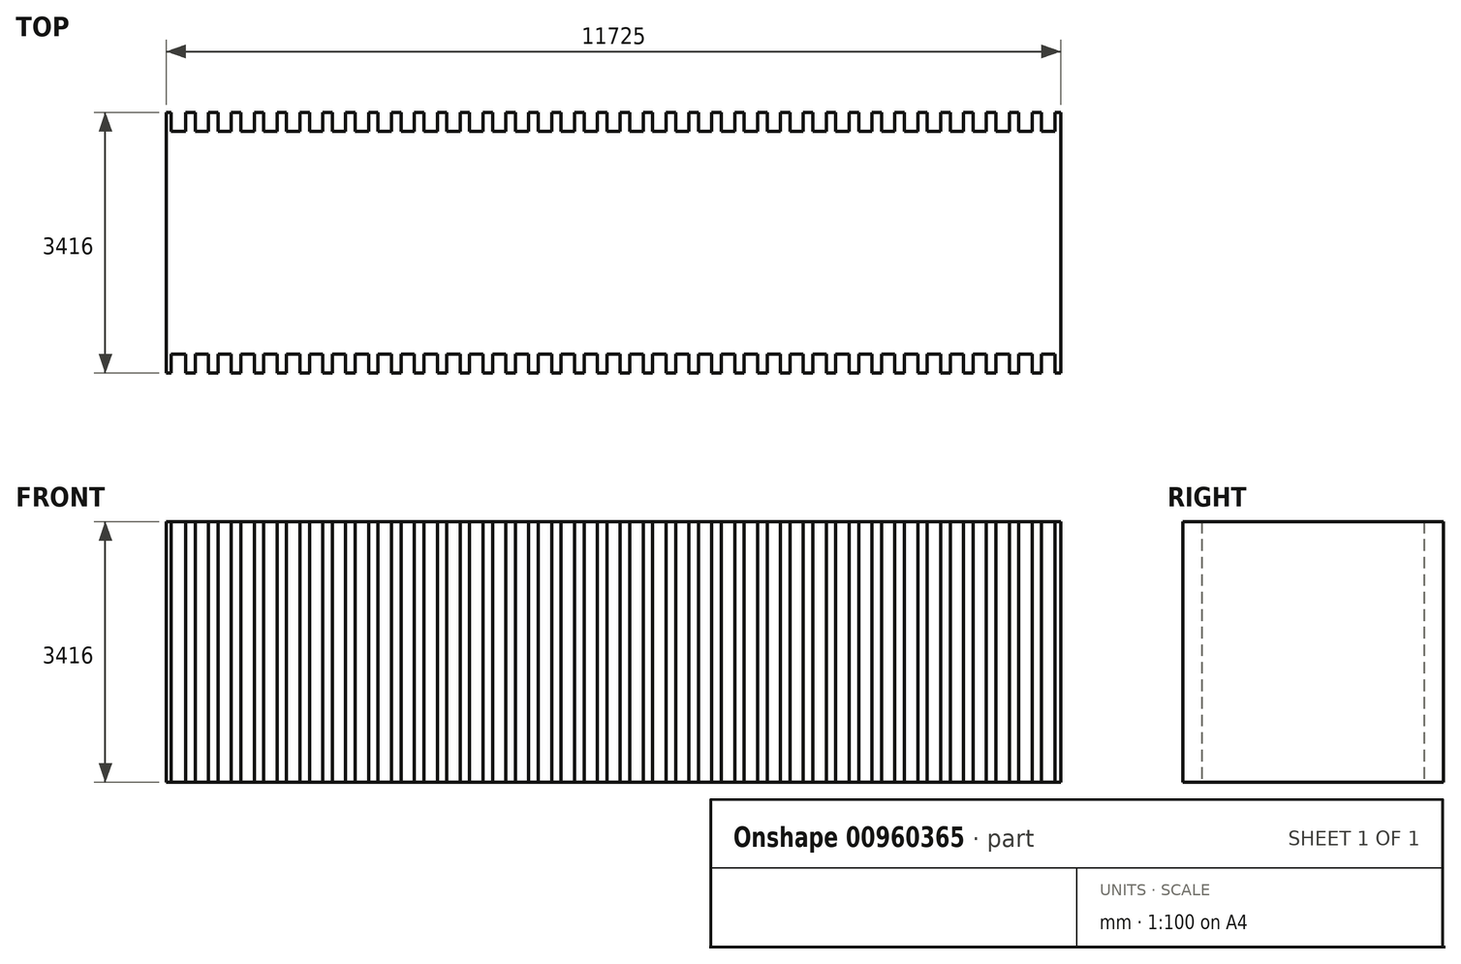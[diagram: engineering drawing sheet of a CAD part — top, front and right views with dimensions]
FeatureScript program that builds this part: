
annotation { "Feature Type Name" : "Feature", "Feature Type Description" : "" }
export const myFeature = defineFeature(function(context is Context, id is Id, definition is map)
    precondition{}
    {
        {
            var Q0;
            Q0=qCreatedBy(makeId("Top.planeOp"),FACE);
            var sketch = newSketch(context, id + "F0", { "sketchPlane" : qUnion([Q0])});
            skLineSegment(sketch, "E0.bottom", {"start": v(-25000, 7300) * mm, "end": v(25000, 7300) * mm});
            skLineSegment(sketch, "E0.top", {"start": v(-25000, -7300) * mm, "end": v(25000, -7300) * mm});
            skLineSegment(sketch, "E0.left", {"start": v(-25000, 7300) * mm, "end": v(-25000, -7300) * mm});
            skLineSegment(sketch, "E0.right", {"start": v(25000, 7300) * mm, "end": v(25000, -7300) * mm});
            skPoint(sketch, "E0.middle", {"position": v(0, 0) * mm});
            skSolve(sketch);
        }
        {
            var Q0;
            Q0=makeQuery(id+"F0.imprint","IMPRINT",FACE,{"disambiguationData":[TD([[makeQuery(id+"F0.imprint","IMPRINT",EDGE,{"derivedFrom":sQuery(id+"F0.wireOp",EDGE,"E0.bottom")}),-1.0]])]});
            var sketch = newSketch(context, id + "F1", { "sketchPlane" : qUnion([Q0])});
            skLineSegment(sketch, "E1", {"start": v(-20201.46, 5909) * mm, "end": v(-20138.96, 5909) * mm});
            skLineSegment(sketch, "E2", {"start": v(-20201.46, 5909) * mm, "end": v(-20201.46, 2493) * mm});
            skLineSegment(sketch, "E3", {"start": v(-20201.46, 2493) * mm, "end": v(-20138.96, 2493) * mm});
            skLineSegment(sketch, "E4", {"start": v(-8476.46, 2493) * mm, "end": v(-8476.46, 5909) * mm});
            skLineSegment(sketch, "E5.0", {"start": v(-20138.96, 5909) * mm, "end": v(-20138.96, 2493) * mm});
            skLineSegment(sketch, "E6.0", {"start": v(-19951.46, 5909) * mm, "end": v(-19951.46, 2493) * mm});
            skLineSegment(sketch, "E7.0", {"start": v(-19651.46, 5909) * mm, "end": v(-19651.46, 2493) * mm});
            skLineSegment(sketch, "E8.0", {"start": v(-19351.46, 5909) * mm, "end": v(-19351.46, 2493) * mm});
            skLineSegment(sketch, "E9.0", {"start": v(-19051.46, 5909) * mm, "end": v(-19051.46, 2493) * mm});
            skLineSegment(sketch, "E10.0", {"start": v(-18751.46, 5909) * mm, "end": v(-18751.46, 2493) * mm});
            skLineSegment(sketch, "E11.0", {"start": v(-18451.46, 5909) * mm, "end": v(-18451.46, 2493) * mm});
            skLineSegment(sketch, "E12.0", {"start": v(-18151.46, 5909) * mm, "end": v(-18151.46, 2493) * mm});
            skLineSegment(sketch, "E13.0", {"start": v(-17851.46, 5909) * mm, "end": v(-17851.46, 2493) * mm});
            skLineSegment(sketch, "E14.0", {"start": v(-17551.46, 5909) * mm, "end": v(-17551.46, 2493) * mm});
            skLineSegment(sketch, "E15.0", {"start": v(-17251.46, 5909) * mm, "end": v(-17251.46, 2493) * mm});
            skLineSegment(sketch, "E16.0", {"start": v(-16951.46, 5909) * mm, "end": v(-16951.46, 2493) * mm});
            skLineSegment(sketch, "E17.0", {"start": v(-16651.46, 5909) * mm, "end": v(-16651.46, 2493) * mm});
            skLineSegment(sketch, "E18.0", {"start": v(-16351.46, 5909) * mm, "end": v(-16351.46, 2493) * mm});
            skLineSegment(sketch, "E19.0", {"start": v(-16051.46, 5909) * mm, "end": v(-16051.46, 2493) * mm});
            skLineSegment(sketch, "E20.0", {"start": v(-15751.46, 5909) * mm, "end": v(-15751.46, 2493) * mm});
            skLineSegment(sketch, "E21.0", {"start": v(-25005, 7305) * mm, "end": v(-25005, -7305) * mm});
            skLineSegment(sketch, "E21.1", {"start": v(25005, 7305) * mm, "end": v(-25005, 7305) * mm});
            skLineSegment(sketch, "E21.2", {"start": v(25005, -7305) * mm, "end": v(25005, 7305) * mm});
            skLineSegment(sketch, "E21.3", {"start": v(-25005, -7305) * mm, "end": v(25005, -7305) * mm});
            skLineSegment(sketch, "E22.0", {"start": v(-15451.46, 5909) * mm, "end": v(-15451.46, 2493) * mm});
            skLineSegment(sketch, "E23.0", {"start": v(-15151.46, 5909) * mm, "end": v(-15151.46, 2493) * mm});
            skLineSegment(sketch, "E24.0", {"start": v(-14851.46, 5909) * mm, "end": v(-14851.46, 2493) * mm});
            skLineSegment(sketch, "E25.0", {"start": v(-14551.46, 5909) * mm, "end": v(-14551.46, 2493) * mm});
            skLineSegment(sketch, "E26.0", {"start": v(-14251.46, 5909) * mm, "end": v(-14251.46, 2493) * mm});
            skLineSegment(sketch, "E27.0", {"start": v(-13951.46, 5909) * mm, "end": v(-13951.46, 2493) * mm});
            skLineSegment(sketch, "E28.0", {"start": v(-13651.46, 5909) * mm, "end": v(-13651.46, 2493) * mm});
            skLineSegment(sketch, "E29.0", {"start": v(-13351.46, 5909) * mm, "end": v(-13351.46, 2493) * mm});
            skLineSegment(sketch, "E30.0", {"start": v(-13051.46, 5909) * mm, "end": v(-13051.46, 2493) * mm});
            skLineSegment(sketch, "E31.0", {"start": v(-12751.46, 5909) * mm, "end": v(-12751.46, 2493) * mm});
            skLineSegment(sketch, "E32.0", {"start": v(-12451.46, 5909) * mm, "end": v(-12451.46, 2493) * mm});
            skLineSegment(sketch, "E33.0", {"start": v(-12151.46, 5909) * mm, "end": v(-12151.46, 2493) * mm});
            skLineSegment(sketch, "E34.0", {"start": v(-11851.46, 5909) * mm, "end": v(-11851.46, 2493) * mm});
            skLineSegment(sketch, "E35.0", {"start": v(-11551.46, 5909) * mm, "end": v(-11551.46, 2493) * mm});
            skLineSegment(sketch, "E36.0", {"start": v(-11251.46, 5909) * mm, "end": v(-11251.46, 2493) * mm});
            skLineSegment(sketch, "E37.0", {"start": v(-10951.46, 5909) * mm, "end": v(-10951.46, 2493) * mm});
            skLineSegment(sketch, "E38.0", {"start": v(-10651.46, 5909) * mm, "end": v(-10651.46, 2493) * mm});
            skLineSegment(sketch, "E39.0", {"start": v(-10351.46, 5909) * mm, "end": v(-10351.46, 2493) * mm});
            skLineSegment(sketch, "E40.0", {"start": v(-10051.46, 5909) * mm, "end": v(-10051.46, 2493) * mm});
            skLineSegment(sketch, "E41.0", {"start": v(-9751.46, 5909) * mm, "end": v(-9751.46, 2493) * mm});
            skLineSegment(sketch, "E42.0", {"start": v(-9451.46, 5909) * mm, "end": v(-9451.46, 2493) * mm});
            skLineSegment(sketch, "E43.0", {"start": v(-9151.46, 5909) * mm, "end": v(-9151.46, 2493) * mm});
            skLineSegment(sketch, "E44.0", {"start": v(-8851.46, 5909) * mm, "end": v(-8851.46, 2493) * mm});
            skLineSegment(sketch, "E45.0", {"start": v(-8551.46, 5909) * mm, "end": v(-8551.46, 2493) * mm});
            skLineSegment(sketch, "E46.0", {"start": v(-19826.46, 5909) * mm, "end": v(-19826.46, 2493) * mm});
            skLineSegment(sketch, "E47.0", {"start": v(-19526.46, 5909) * mm, "end": v(-19526.46, 2493) * mm});
            skLineSegment(sketch, "E48.0", {"start": v(-19226.46, 5909) * mm, "end": v(-19226.46, 2493) * mm});
            skLineSegment(sketch, "E49.0", {"start": v(-18926.46, 5909) * mm, "end": v(-18926.46, 2493) * mm});
            skLineSegment(sketch, "E50.0", {"start": v(-18626.46, 5909) * mm, "end": v(-18626.46, 2493) * mm});
            skLineSegment(sketch, "E51.0", {"start": v(-18326.46, 5909) * mm, "end": v(-18326.46, 2493) * mm});
            skLineSegment(sketch, "E52.0", {"start": v(-18026.46, 5909) * mm, "end": v(-18026.46, 2493) * mm});
            skLineSegment(sketch, "E53.0", {"start": v(-17726.46, 5909) * mm, "end": v(-17726.46, 2493) * mm});
            skLineSegment(sketch, "E54.0", {"start": v(-17426.46, 5909) * mm, "end": v(-17426.46, 2493) * mm});
            skLineSegment(sketch, "E55.0", {"start": v(-17126.46, 5909) * mm, "end": v(-17126.46, 2493) * mm});
            skLineSegment(sketch, "E56.0", {"start": v(-16826.46, 5909) * mm, "end": v(-16826.46, 2493) * mm});
            skLineSegment(sketch, "E57.0", {"start": v(-16526.46, 5909) * mm, "end": v(-16526.46, 2493) * mm});
            skLineSegment(sketch, "E58.0", {"start": v(-16226.46, 5909) * mm, "end": v(-16226.46, 2493) * mm});
            skLineSegment(sketch, "E59.0", {"start": v(-15926.46, 5909) * mm, "end": v(-15926.46, 2493) * mm});
            skLineSegment(sketch, "E60.0", {"start": v(-15626.46, 5909) * mm, "end": v(-15626.46, 2493) * mm});
            skLineSegment(sketch, "E61.0", {"start": v(-15326.46, 5909) * mm, "end": v(-15326.46, 2493) * mm});
            skLineSegment(sketch, "E62.0", {"start": v(-15026.46, 5909) * mm, "end": v(-15026.46, 2493) * mm});
            skLineSegment(sketch, "E63.0", {"start": v(-14726.46, 5909) * mm, "end": v(-14726.46, 2493) * mm});
            skLineSegment(sketch, "E64.0", {"start": v(-14426.46, 5909) * mm, "end": v(-14426.46, 2493) * mm});
            skLineSegment(sketch, "E65.0", {"start": v(-14126.46, 5909) * mm, "end": v(-14126.46, 2493) * mm});
            skLineSegment(sketch, "E66.0", {"start": v(-13826.46, 5909) * mm, "end": v(-13826.46, 2493) * mm});
            skLineSegment(sketch, "E67.0", {"start": v(-13526.46, 5909) * mm, "end": v(-13526.46, 2493) * mm});
            skLineSegment(sketch, "E68.0", {"start": v(-13226.46, 5909) * mm, "end": v(-13226.46, 2493) * mm});
            skLineSegment(sketch, "E69.0", {"start": v(-12926.46, 5909) * mm, "end": v(-12926.46, 2493) * mm});
            skLineSegment(sketch, "E70.0", {"start": v(-12626.46, 5909) * mm, "end": v(-12626.46, 2493) * mm});
            skLineSegment(sketch, "E71.0", {"start": v(-12326.46, 5909) * mm, "end": v(-12326.46, 2493) * mm});
            skLineSegment(sketch, "E72.0", {"start": v(-12026.46, 5909) * mm, "end": v(-12026.46, 2493) * mm});
            skLineSegment(sketch, "E73.0", {"start": v(-11726.46, 5909) * mm, "end": v(-11726.46, 2493) * mm});
            skLineSegment(sketch, "E74.0", {"start": v(-11426.46, 5909) * mm, "end": v(-11426.46, 2493) * mm});
            skLineSegment(sketch, "E75.0", {"start": v(-11126.46, 5909) * mm, "end": v(-11126.46, 2493) * mm});
            skLineSegment(sketch, "E76.0", {"start": v(-10826.46, 5909) * mm, "end": v(-10826.46, 2493) * mm});
            skLineSegment(sketch, "E77.0", {"start": v(-10526.46, 5909) * mm, "end": v(-10526.46, 2493) * mm});
            skLineSegment(sketch, "E78.0", {"start": v(-10226.46, 5909) * mm, "end": v(-10226.46, 2493) * mm});
            skLineSegment(sketch, "E79.0", {"start": v(-9926.46, 5909) * mm, "end": v(-9926.46, 2493) * mm});
            skLineSegment(sketch, "E80.0", {"start": v(-9626.46, 5909) * mm, "end": v(-9626.46, 2493) * mm});
            skLineSegment(sketch, "E81.0", {"start": v(-9326.46, 5909) * mm, "end": v(-9326.46, 2493) * mm});
            skLineSegment(sketch, "E82.0", {"start": v(-9026.46, 5909) * mm, "end": v(-9026.46, 2493) * mm});
            skLineSegment(sketch, "E83.0", {"start": v(-8726.46, 5909) * mm, "end": v(-8726.46, 2493) * mm});
            skLineSegment(sketch, "E84", {"start": v(-20201.46, 5659) * mm, "end": v(-8476.46, 5659) * mm});
            skLineSegment(sketch, "E85", {"start": v(-20201.46, 2743) * mm, "end": v(-8476.46, 2743) * mm});
            skLineSegment(sketch, "E86.trimOffspring", {"start": v(-8551.46, 5909) * mm, "end": v(-8476.46, 5909) * mm});
            skLineSegment(sketch, "E87.trimOffspring", {"start": v(-8851.46, 5909) * mm, "end": v(-8726.46, 5909) * mm});
            skLineSegment(sketch, "E88.trimOffspring", {"start": v(-9151.46, 5909) * mm, "end": v(-9026.46, 5909) * mm});
            skLineSegment(sketch, "E89.trimOffspring", {"start": v(-9451.46, 5909) * mm, "end": v(-9326.46, 5909) * mm});
            skLineSegment(sketch, "E90.trimOffspring", {"start": v(-9751.46, 5909) * mm, "end": v(-9626.46, 5909) * mm});
            skLineSegment(sketch, "E91.trimOffspring", {"start": v(-10051.46, 5909) * mm, "end": v(-9926.46, 5909) * mm});
            skLineSegment(sketch, "E92.trimOffspring", {"start": v(-10351.46, 5909) * mm, "end": v(-10226.46, 5909) * mm});
            skLineSegment(sketch, "E93.trimOffspring", {"start": v(-10651.46, 5909) * mm, "end": v(-10526.46, 5909) * mm});
            skLineSegment(sketch, "E94.trimOffspring", {"start": v(-10951.46, 5909) * mm, "end": v(-10826.46, 5909) * mm});
            skLineSegment(sketch, "E95.trimOffspring", {"start": v(-11251.46, 5909) * mm, "end": v(-11126.46, 5909) * mm});
            skLineSegment(sketch, "E96.trimOffspring", {"start": v(-11551.46, 5909) * mm, "end": v(-11426.46, 5909) * mm});
            skLineSegment(sketch, "E97.trimOffspring", {"start": v(-11851.46, 5909) * mm, "end": v(-11726.46, 5909) * mm});
            skLineSegment(sketch, "E98.trimOffspring", {"start": v(-12151.46, 5909) * mm, "end": v(-12026.46, 5909) * mm});
            skLineSegment(sketch, "E99.trimOffspring", {"start": v(-12451.46, 5909) * mm, "end": v(-12326.46, 5909) * mm});
            skLineSegment(sketch, "E100.trimOffspring", {"start": v(-12751.46, 5909) * mm, "end": v(-12626.46, 5909) * mm});
            skLineSegment(sketch, "E101.trimOffspring", {"start": v(-13051.46, 5909) * mm, "end": v(-12926.46, 5909) * mm});
            skLineSegment(sketch, "E102.trimOffspring", {"start": v(-13351.46, 5909) * mm, "end": v(-13226.46, 5909) * mm});
            skLineSegment(sketch, "E103.trimOffspring", {"start": v(-13651.46, 5909) * mm, "end": v(-13526.46, 5909) * mm});
            skLineSegment(sketch, "E104.trimOffspring", {"start": v(-13951.46, 5909) * mm, "end": v(-13826.46, 5909) * mm});
            skLineSegment(sketch, "E105.trimOffspring", {"start": v(-14251.46, 5909) * mm, "end": v(-14126.46, 5909) * mm});
            skLineSegment(sketch, "E106.trimOffspring", {"start": v(-14551.46, 5909) * mm, "end": v(-14426.46, 5909) * mm});
            skLineSegment(sketch, "E107.trimOffspring", {"start": v(-14851.46, 5909) * mm, "end": v(-14726.46, 5909) * mm});
            skLineSegment(sketch, "E108.trimOffspring", {"start": v(-15151.46, 5909) * mm, "end": v(-15026.46, 5909) * mm});
            skLineSegment(sketch, "E109.trimOffspring", {"start": v(-15451.46, 5909) * mm, "end": v(-15326.46, 5909) * mm});
            skLineSegment(sketch, "E110.trimOffspring", {"start": v(-15751.46, 5909) * mm, "end": v(-15626.46, 5909) * mm});
            skLineSegment(sketch, "E111.trimOffspring", {"start": v(-16051.46, 5909) * mm, "end": v(-15926.46, 5909) * mm});
            skLineSegment(sketch, "E112.trimOffspring", {"start": v(-16351.46, 5909) * mm, "end": v(-16226.46, 5909) * mm});
            skLineSegment(sketch, "E113.trimOffspring", {"start": v(-16651.46, 5909) * mm, "end": v(-16526.46, 5909) * mm});
            skLineSegment(sketch, "E114.trimOffspring", {"start": v(-16951.46, 5909) * mm, "end": v(-16826.46, 5909) * mm});
            skLineSegment(sketch, "E115.trimOffspring", {"start": v(-17251.46, 5909) * mm, "end": v(-17126.46, 5909) * mm});
            skLineSegment(sketch, "E116.trimOffspring", {"start": v(-17551.46, 5909) * mm, "end": v(-17426.46, 5909) * mm});
            skLineSegment(sketch, "E117.trimOffspring", {"start": v(-17851.46, 5909) * mm, "end": v(-17726.46, 5909) * mm});
            skLineSegment(sketch, "E118.trimOffspring", {"start": v(-18151.46, 5909) * mm, "end": v(-18026.46, 5909) * mm});
            skLineSegment(sketch, "E119.trimOffspring", {"start": v(-18451.46, 5909) * mm, "end": v(-18326.46, 5909) * mm});
            skLineSegment(sketch, "E120.trimOffspring", {"start": v(-18751.46, 5909) * mm, "end": v(-18626.46, 5909) * mm});
            skLineSegment(sketch, "E121.trimOffspring", {"start": v(-19051.46, 5909) * mm, "end": v(-18926.46, 5909) * mm});
            skLineSegment(sketch, "E122.trimOffspring", {"start": v(-19351.46, 5909) * mm, "end": v(-19226.46, 5909) * mm});
            skLineSegment(sketch, "E123.trimOffspring", {"start": v(-19651.46, 5909) * mm, "end": v(-19526.46, 5909) * mm});
            skLineSegment(sketch, "E124.trimOffspring", {"start": v(-19951.46, 5909) * mm, "end": v(-19826.46, 5909) * mm});
            skLineSegment(sketch, "E125.trimOffspring", {"start": v(-19651.46, 2493) * mm, "end": v(-19526.46, 2493) * mm});
            skLineSegment(sketch, "E126.trimOffspring", {"start": v(-18751.46, 2493) * mm, "end": v(-18626.46, 2493) * mm});
            skLineSegment(sketch, "E127.trimOffspring", {"start": v(-17851.46, 2493) * mm, "end": v(-17726.46, 2493) * mm});
            skLineSegment(sketch, "E128.trimOffspring", {"start": v(-17251.46, 2493) * mm, "end": v(-17126.46, 2493) * mm});
            skLineSegment(sketch, "E129.trimOffspring", {"start": v(-16351.46, 2493) * mm, "end": v(-16226.46, 2493) * mm});
            skLineSegment(sketch, "E130.trimOffspring", {"start": v(-16951.46, 2493) * mm, "end": v(-16826.46, 2493) * mm});
            skLineSegment(sketch, "E131", {"start": v(-17551.46, 2493) * mm, "end": v(-17426.46, 2493) * mm});
            skLineSegment(sketch, "E132", {"start": v(-16651.46, 2493) * mm, "end": v(-16526.46, 2493) * mm});
            skLineSegment(sketch, "E133.trimOffspring", {"start": v(-15751.46, 2493) * mm, "end": v(-15626.46, 2493) * mm});
            skLineSegment(sketch, "E134.trimOffspring", {"start": v(-14551.46, 2493) * mm, "end": v(-14426.46, 2493) * mm});
            skLineSegment(sketch, "E135.trimOffspring", {"start": v(-15151.46, 2493) * mm, "end": v(-15026.46, 2493) * mm});
            skLineSegment(sketch, "E136.trimOffspring", {"start": v(-15451.46, 2493) * mm, "end": v(-15326.46, 2493) * mm});
            skLineSegment(sketch, "E137", {"start": v(-14851.46, 2493) * mm, "end": v(-14726.46, 2493) * mm});
            skLineSegment(sketch, "E138.trimOffspring", {"start": v(-13951.46, 2493) * mm, "end": v(-13826.46, 2493) * mm});
            skLineSegment(sketch, "E139.trimOffspring", {"start": v(-13351.46, 2493) * mm, "end": v(-13226.46, 2493) * mm});
            skLineSegment(sketch, "E140.trimOffspring", {"start": v(-13651.46, 2493) * mm, "end": v(-13526.46, 2493) * mm});
            skLineSegment(sketch, "E141", {"start": v(-14251.46, 2493) * mm, "end": v(-14126.46, 2493) * mm});
            skLineSegment(sketch, "E142.trimOffspring", {"start": v(-13051.46, 2493) * mm, "end": v(-12926.46, 2493) * mm});
            skLineSegment(sketch, "E143.trimOffspring", {"start": v(-12751.46, 2493) * mm, "end": v(-12626.46, 2493) * mm});
            skLineSegment(sketch, "E144.trimOffspring", {"start": v(-12151.46, 2493) * mm, "end": v(-12026.46, 2493) * mm});
            skLineSegment(sketch, "E145.trimOffspring", {"start": v(-11551.46, 2493) * mm, "end": v(-11426.46, 2493) * mm});
            skLineSegment(sketch, "E146.trimOffspring", {"start": v(-11851.46, 2493) * mm, "end": v(-11726.46, 2493) * mm});
            skLineSegment(sketch, "E147.trimOffspring", {"start": v(-11251.46, 2493) * mm, "end": v(-11126.46, 2493) * mm});
            skLineSegment(sketch, "E148.trimOffspring", {"start": v(-10951.46, 2493) * mm, "end": v(-10826.46, 2493) * mm});
            skLineSegment(sketch, "E149.trimOffspring", {"start": v(-10651.46, 2493) * mm, "end": v(-10526.46, 2493) * mm});
            skLineSegment(sketch, "E150.trimOffspring", {"start": v(-9751.46, 2493) * mm, "end": v(-9626.46, 2493) * mm});
            skLineSegment(sketch, "E151.trimOffspring", {"start": v(-8851.46, 2493) * mm, "end": v(-8726.46, 2493) * mm});
            skLineSegment(sketch, "E152", {"start": v(-10351.46, 2493) * mm, "end": v(-10226.46, 2493) * mm});
            skLineSegment(sketch, "E153", {"start": v(-10051.46, 2493) * mm, "end": v(-9926.46, 2493) * mm});
            skLineSegment(sketch, "E154", {"start": v(-9151.46, 2493) * mm, "end": v(-9026.46, 2493) * mm});
            skLineSegment(sketch, "E155.trimOffspring", {"start": v(-9451.46, 2493) * mm, "end": v(-9326.46, 2493) * mm});
            skLineSegment(sketch, "E156.trimOffspring", {"start": v(-8551.46, 2493) * mm, "end": v(-8476.46, 2493) * mm});
            skLineSegment(sketch, "E157.trimOffspring", {"start": v(-18451.46, 2493) * mm, "end": v(-18326.46, 2493) * mm});
            skLineSegment(sketch, "E158.trimOffspring", {"start": v(-19351.46, 2493) * mm, "end": v(-19226.46, 2493) * mm});
            skLineSegment(sketch, "E159", {"start": v(-19051.46, 2493) * mm, "end": v(-18926.46, 2493) * mm});
            skLineSegment(sketch, "E160", {"start": v(-18151.46, 2493) * mm, "end": v(-18026.46, 2493) * mm});
            skLineSegment(sketch, "E161", {"start": v(-16051.46, 2493) * mm, "end": v(-15926.46, 2493) * mm});
            skLineSegment(sketch, "E162", {"start": v(-19951.46, 2493) * mm, "end": v(-19826.46, 2493) * mm});
            skLineSegment(sketch, "E163", {"start": v(-12451.46, 2493) * mm, "end": v(-12326.46, 2493) * mm});
            skSolve(sketch);
        }
        {
            var Q0;
            {var subQ0=sQuery(id+"F1.wireOp",EDGE,"E88.trimOffspring");Q0=makeQuery(id+"F1.imprint","IMPRINT",FACE,{"disambiguationData":[TD([[makeQuery(id+"F1.imprint","IMPRINT",EDGE,{"derivedFrom":subQ0}),-1.0]])]});}
            var Q1;
            {var subQ0=sQuery(id+"F1.wireOp",EDGE,"E112.trimOffspring");Q1=makeQuery(id+"F1.imprint","IMPRINT",FACE,{"disambiguationData":[TD([[makeQuery(id+"F1.imprint","IMPRINT",EDGE,{"derivedFrom":subQ0}),-1.0]])]});}
            var Q2;
            {var subQ0=sQuery(id+"F1.wireOp",EDGE,"E84");var subQ1=sQuery(id+"F1.wireOp",EDGE,"E38.0");var subQ2=makeQuery(id+"F1.imprint","INTERSECT",VERTEX,{"derivedFrom":[subQ1,subQ0]});Q2=makeQuery(id+"F1.imprint","IMPRINT",FACE,{"disambiguationData":[TD([[makeQuery(id+"F1.imprint","IMPRINT",EDGE,{"disambiguationData":[TD([[subQ2,-1.0]])],"derivedFrom":subQ1}),1.0]])]});}
            var Q3;
            {var subQ0=sQuery(id+"F1.wireOp",EDGE,"E158.trimOffspring");Q3=makeQuery(id+"F1.imprint","IMPRINT",FACE,{"disambiguationData":[TD([[makeQuery(id+"F1.imprint","IMPRINT",EDGE,{"derivedFrom":subQ0}),1.0]])]});}
            var Q4;
            {var subQ0=sQuery(id+"F1.wireOp",EDGE,"E84");var subQ1=sQuery(id+"F1.wireOp",EDGE,"E18.0");var subQ2=makeQuery(id+"F1.imprint","INTERSECT",VERTEX,{"derivedFrom":[subQ1,subQ0]});Q4=makeQuery(id+"F1.imprint","IMPRINT",FACE,{"disambiguationData":[TD([[makeQuery(id+"F1.imprint","IMPRINT",EDGE,{"disambiguationData":[TD([[subQ2,-1.0]])],"derivedFrom":subQ1}),-1.0]])]});}
            var Q5;
            {var subQ0=sQuery(id+"F1.wireOp",EDGE,"E140.trimOffspring");Q5=makeQuery(id+"F1.imprint","IMPRINT",FACE,{"disambiguationData":[TD([[makeQuery(id+"F1.imprint","IMPRINT",EDGE,{"derivedFrom":subQ0}),1.0]])]});}
            var Q6;
            {var subQ0=sQuery(id+"F1.wireOp",EDGE,"E84");var subQ1=sQuery(id+"F1.wireOp",EDGE,"E35.0");var subQ2=makeQuery(id+"F1.imprint","INTERSECT",VERTEX,{"derivedFrom":[subQ1,subQ0]});Q6=makeQuery(id+"F1.imprint","IMPRINT",FACE,{"disambiguationData":[TD([[makeQuery(id+"F1.imprint","IMPRINT",EDGE,{"disambiguationData":[TD([[subQ2,-1.0]])],"derivedFrom":subQ1}),-1.0]])]});}
            var Q7;
            {var subQ0=sQuery(id+"F1.wireOp",EDGE,"E107.trimOffspring");Q7=makeQuery(id+"F1.imprint","IMPRINT",FACE,{"disambiguationData":[TD([[makeQuery(id+"F1.imprint","IMPRINT",EDGE,{"derivedFrom":subQ0}),-1.0]])]});}
            var Q8;
            {var subQ0=sQuery(id+"F1.wireOp",EDGE,"E129.trimOffspring");Q8=makeQuery(id+"F1.imprint","IMPRINT",FACE,{"disambiguationData":[TD([[makeQuery(id+"F1.imprint","IMPRINT",EDGE,{"derivedFrom":subQ0}),1.0]])]});}
            var Q9;
            {var subQ0=sQuery(id+"F1.wireOp",EDGE,"E120.trimOffspring");Q9=makeQuery(id+"F1.imprint","IMPRINT",FACE,{"disambiguationData":[TD([[makeQuery(id+"F1.imprint","IMPRINT",EDGE,{"derivedFrom":subQ0}),-1.0]])]});}
            var Q10;
            {var subQ0=sQuery(id+"F1.wireOp",EDGE,"E115.trimOffspring");Q10=makeQuery(id+"F1.imprint","IMPRINT",FACE,{"disambiguationData":[TD([[makeQuery(id+"F1.imprint","IMPRINT",EDGE,{"derivedFrom":subQ0}),-1.0]])]});}
            var Q11;
            {var subQ0=sQuery(id+"F1.wireOp",EDGE,"E138.trimOffspring");Q11=makeQuery(id+"F1.imprint","IMPRINT",FACE,{"disambiguationData":[TD([[makeQuery(id+"F1.imprint","IMPRINT",EDGE,{"derivedFrom":subQ0}),1.0]])]});}
            var Q12;
            {var subQ0=sQuery(id+"F1.wireOp",EDGE,"E84");var subQ1=sQuery(id+"F1.wireOp",EDGE,"E11.0");var subQ2=makeQuery(id+"F1.imprint","INTERSECT",VERTEX,{"derivedFrom":[subQ1,subQ0]});Q12=makeQuery(id+"F1.imprint","IMPRINT",FACE,{"disambiguationData":[TD([[makeQuery(id+"F1.imprint","IMPRINT",EDGE,{"disambiguationData":[TD([[subQ2,-1.0]])],"derivedFrom":subQ1}),1.0]])]});}
            var Q13;
            {var subQ0=sQuery(id+"F1.wireOp",EDGE,"E91.trimOffspring");Q13=makeQuery(id+"F1.imprint","IMPRINT",FACE,{"disambiguationData":[TD([[makeQuery(id+"F1.imprint","IMPRINT",EDGE,{"derivedFrom":subQ0}),-1.0]])]});}
            var Q14;
            {var subQ0=sQuery(id+"F1.wireOp",EDGE,"E84");var subQ1=sQuery(id+"F1.wireOp",EDGE,"E13.0");var subQ2=makeQuery(id+"F1.imprint","INTERSECT",VERTEX,{"derivedFrom":[subQ1,subQ0]});Q14=makeQuery(id+"F1.imprint","IMPRINT",FACE,{"disambiguationData":[TD([[makeQuery(id+"F1.imprint","IMPRINT",EDGE,{"disambiguationData":[TD([[subQ2,-1.0]])],"derivedFrom":subQ1}),-1.0]])]});}
            var Q15;
            {var subQ0=sQuery(id+"F1.wireOp",EDGE,"E84");var subQ1=sQuery(id+"F1.wireOp",EDGE,"E26.0");var subQ2=makeQuery(id+"F1.imprint","INTERSECT",VERTEX,{"derivedFrom":[subQ1,subQ0]});Q15=makeQuery(id+"F1.imprint","IMPRINT",FACE,{"disambiguationData":[TD([[makeQuery(id+"F1.imprint","IMPRINT",EDGE,{"disambiguationData":[TD([[subQ2,-1.0]])],"derivedFrom":subQ1}),-1.0]])]});}
            var Q16;
            {var subQ0=sQuery(id+"F1.wireOp",EDGE,"E121.trimOffspring");Q16=makeQuery(id+"F1.imprint","IMPRINT",FACE,{"disambiguationData":[TD([[makeQuery(id+"F1.imprint","IMPRINT",EDGE,{"derivedFrom":subQ0}),-1.0]])]});}
            var Q17;
            {var subQ0=sQuery(id+"F1.wireOp",EDGE,"E130.trimOffspring");Q17=makeQuery(id+"F1.imprint","IMPRINT",FACE,{"disambiguationData":[TD([[makeQuery(id+"F1.imprint","IMPRINT",EDGE,{"derivedFrom":subQ0}),1.0]])]});}
            var Q18;
            {var subQ0=sQuery(id+"F1.wireOp",EDGE,"E154");Q18=makeQuery(id+"F1.imprint","IMPRINT",FACE,{"disambiguationData":[TD([[makeQuery(id+"F1.imprint","IMPRINT",EDGE,{"derivedFrom":subQ0}),1.0]])]});}
            var Q19;
            {var subQ0=sQuery(id+"F1.wireOp",EDGE,"E151.trimOffspring");Q19=makeQuery(id+"F1.imprint","IMPRINT",FACE,{"disambiguationData":[TD([[makeQuery(id+"F1.imprint","IMPRINT",EDGE,{"derivedFrom":subQ0}),1.0]])]});}
            var Q20;
            {var subQ0=sQuery(id+"F1.wireOp",EDGE,"E84");var subQ1=sQuery(id+"F1.wireOp",EDGE,"E30.0");var subQ2=makeQuery(id+"F1.imprint","INTERSECT",VERTEX,{"derivedFrom":[subQ1,subQ0]});Q20=makeQuery(id+"F1.imprint","IMPRINT",FACE,{"disambiguationData":[TD([[makeQuery(id+"F1.imprint","IMPRINT",EDGE,{"disambiguationData":[TD([[subQ2,-1.0]])],"derivedFrom":subQ1}),-1.0]])]});}
            var Q21;
            {var subQ0=sQuery(id+"F1.wireOp",EDGE,"E84");var subQ1=sQuery(id+"F1.wireOp",EDGE,"E19.0");var subQ2=makeQuery(id+"F1.imprint","INTERSECT",VERTEX,{"derivedFrom":[subQ1,subQ0]});Q21=makeQuery(id+"F1.imprint","IMPRINT",FACE,{"disambiguationData":[TD([[makeQuery(id+"F1.imprint","IMPRINT",EDGE,{"disambiguationData":[TD([[subQ2,-1.0]])],"derivedFrom":subQ1}),1.0]])]});}
            var Q22;
            {var subQ0=sQuery(id+"F1.wireOp",EDGE,"E84");var subQ1=sQuery(id+"F1.wireOp",EDGE,"E14.0");var subQ2=makeQuery(id+"F1.imprint","INTERSECT",VERTEX,{"derivedFrom":[subQ1,subQ0]});Q22=makeQuery(id+"F1.imprint","IMPRINT",FACE,{"disambiguationData":[TD([[makeQuery(id+"F1.imprint","IMPRINT",EDGE,{"disambiguationData":[TD([[subQ2,-1.0]])],"derivedFrom":subQ1}),-1.0]])]});}
            var Q23;
            {var subQ0=sQuery(id+"F1.wireOp",EDGE,"E84");var subQ1=sQuery(id+"F1.wireOp",EDGE,"E12.0");var subQ2=makeQuery(id+"F1.imprint","INTERSECT",VERTEX,{"derivedFrom":[subQ1,subQ0]});Q23=makeQuery(id+"F1.imprint","IMPRINT",FACE,{"disambiguationData":[TD([[makeQuery(id+"F1.imprint","IMPRINT",EDGE,{"disambiguationData":[TD([[subQ2,-1.0]])],"derivedFrom":subQ1}),1.0]])]});}
            var Q24;
            {var subQ0=sQuery(id+"F1.wireOp",EDGE,"E143.trimOffspring");Q24=makeQuery(id+"F1.imprint","IMPRINT",FACE,{"disambiguationData":[TD([[makeQuery(id+"F1.imprint","IMPRINT",EDGE,{"derivedFrom":subQ0}),1.0]])]});}
            var Q25;
            {var subQ0=sQuery(id+"F1.wireOp",EDGE,"E161");Q25=makeQuery(id+"F1.imprint","IMPRINT",FACE,{"disambiguationData":[TD([[makeQuery(id+"F1.imprint","IMPRINT",EDGE,{"derivedFrom":subQ0}),1.0]])]});}
            var Q26;
            {var subQ0=sQuery(id+"F1.wireOp",EDGE,"E100.trimOffspring");Q26=makeQuery(id+"F1.imprint","IMPRINT",FACE,{"disambiguationData":[TD([[makeQuery(id+"F1.imprint","IMPRINT",EDGE,{"derivedFrom":subQ0}),-1.0]])]});}
            var Q27;
            {var subQ0=sQuery(id+"F1.wireOp",EDGE,"E84");var subQ1=sQuery(id+"F1.wireOp",EDGE,"E15.0");var subQ2=makeQuery(id+"F1.imprint","INTERSECT",VERTEX,{"derivedFrom":[subQ1,subQ0]});Q27=makeQuery(id+"F1.imprint","IMPRINT",FACE,{"disambiguationData":[TD([[makeQuery(id+"F1.imprint","IMPRINT",EDGE,{"disambiguationData":[TD([[subQ2,-1.0]])],"derivedFrom":subQ1}),-1.0]])]});}
            var Q28;
            {var subQ0=sQuery(id+"F1.wireOp",EDGE,"E84");var subQ1=sQuery(id+"F1.wireOp",EDGE,"E39.0");var subQ2=makeQuery(id+"F1.imprint","INTERSECT",VERTEX,{"derivedFrom":[subQ1,subQ0]});Q28=makeQuery(id+"F1.imprint","IMPRINT",FACE,{"disambiguationData":[TD([[makeQuery(id+"F1.imprint","IMPRINT",EDGE,{"disambiguationData":[TD([[subQ2,-1.0]])],"derivedFrom":subQ1}),1.0]])]});}
            var Q29;
            {var subQ0=sQuery(id+"F1.wireOp",EDGE,"E84");var subQ1=sQuery(id+"F1.wireOp",EDGE,"E36.0");var subQ2=makeQuery(id+"F1.imprint","INTERSECT",VERTEX,{"derivedFrom":[subQ1,subQ0]});Q29=makeQuery(id+"F1.imprint","IMPRINT",FACE,{"disambiguationData":[TD([[makeQuery(id+"F1.imprint","IMPRINT",EDGE,{"disambiguationData":[TD([[subQ2,-1.0]])],"derivedFrom":subQ1}),1.0]])]});}
            var Q30;
            {var subQ0=sQuery(id+"F1.wireOp",EDGE,"E84");var subQ1=sQuery(id+"F1.wireOp",EDGE,"E40.0");var subQ2=makeQuery(id+"F1.imprint","INTERSECT",VERTEX,{"derivedFrom":[subQ1,subQ0]});Q30=makeQuery(id+"F1.imprint","IMPRINT",FACE,{"disambiguationData":[TD([[makeQuery(id+"F1.imprint","IMPRINT",EDGE,{"disambiguationData":[TD([[subQ2,-1.0]])],"derivedFrom":subQ1}),1.0]])]});}
            var Q31;
            {var subQ0=sQuery(id+"F1.wireOp",EDGE,"E118.trimOffspring");Q31=makeQuery(id+"F1.imprint","IMPRINT",FACE,{"disambiguationData":[TD([[makeQuery(id+"F1.imprint","IMPRINT",EDGE,{"derivedFrom":subQ0}),-1.0]])]});}
            var Q32;
            {var subQ0=sQuery(id+"F1.wireOp",EDGE,"E84");var subQ1=sQuery(id+"F1.wireOp",EDGE,"E10.0");var subQ2=makeQuery(id+"F1.imprint","INTERSECT",VERTEX,{"derivedFrom":[subQ1,subQ0]});Q32=makeQuery(id+"F1.imprint","IMPRINT",FACE,{"disambiguationData":[TD([[makeQuery(id+"F1.imprint","IMPRINT",EDGE,{"disambiguationData":[TD([[subQ2,-1.0]])],"derivedFrom":subQ1}),-1.0]])]});}
            var Q33;
            {var subQ0=sQuery(id+"F1.wireOp",EDGE,"E84");var subQ1=sQuery(id+"F1.wireOp",EDGE,"E19.0");var subQ2=makeQuery(id+"F1.imprint","INTERSECT",VERTEX,{"derivedFrom":[subQ1,subQ0]});Q33=makeQuery(id+"F1.imprint","IMPRINT",FACE,{"disambiguationData":[TD([[makeQuery(id+"F1.imprint","IMPRINT",EDGE,{"disambiguationData":[TD([[subQ2,-1.0]])],"derivedFrom":subQ1}),-1.0]])]});}
            var Q34;
            {var subQ0=sQuery(id+"F1.wireOp",EDGE,"E84");var subQ1=sQuery(id+"F1.wireOp",EDGE,"E29.0");var subQ2=makeQuery(id+"F1.imprint","INTERSECT",VERTEX,{"derivedFrom":[subQ1,subQ0]});Q34=makeQuery(id+"F1.imprint","IMPRINT",FACE,{"disambiguationData":[TD([[makeQuery(id+"F1.imprint","IMPRINT",EDGE,{"disambiguationData":[TD([[subQ2,-1.0]])],"derivedFrom":subQ1}),-1.0]])]});}
            var Q35;
            {var subQ0=sQuery(id+"F1.wireOp",EDGE,"E84");var subQ1=sQuery(id+"F1.wireOp",EDGE,"E9.0");var subQ2=makeQuery(id+"F1.imprint","INTERSECT",VERTEX,{"derivedFrom":[subQ1,subQ0]});Q35=makeQuery(id+"F1.imprint","IMPRINT",FACE,{"disambiguationData":[TD([[makeQuery(id+"F1.imprint","IMPRINT",EDGE,{"disambiguationData":[TD([[subQ2,-1.0]])],"derivedFrom":subQ1}),-1.0]])]});}
            var Q36;
            {var subQ0=sQuery(id+"F1.wireOp",EDGE,"E102.trimOffspring");Q36=makeQuery(id+"F1.imprint","IMPRINT",FACE,{"disambiguationData":[TD([[makeQuery(id+"F1.imprint","IMPRINT",EDGE,{"derivedFrom":subQ0}),-1.0]])]});}
            var Q37;
            {var subQ0=sQuery(id+"F1.wireOp",EDGE,"E99.trimOffspring");Q37=makeQuery(id+"F1.imprint","IMPRINT",FACE,{"disambiguationData":[TD([[makeQuery(id+"F1.imprint","IMPRINT",EDGE,{"derivedFrom":subQ0}),-1.0]])]});}
            var Q38;
            {var subQ0=sQuery(id+"F1.wireOp",EDGE,"E117.trimOffspring");Q38=makeQuery(id+"F1.imprint","IMPRINT",FACE,{"disambiguationData":[TD([[makeQuery(id+"F1.imprint","IMPRINT",EDGE,{"derivedFrom":subQ0}),-1.0]])]});}
            var Q39;
            {var subQ0=sQuery(id+"F1.wireOp",EDGE,"E84");var subQ1=sQuery(id+"F1.wireOp",EDGE,"E17.0");var subQ2=makeQuery(id+"F1.imprint","INTERSECT",VERTEX,{"derivedFrom":[subQ1,subQ0]});Q39=makeQuery(id+"F1.imprint","IMPRINT",FACE,{"disambiguationData":[TD([[makeQuery(id+"F1.imprint","IMPRINT",EDGE,{"disambiguationData":[TD([[subQ2,-1.0]])],"derivedFrom":subQ1}),-1.0]])]});}
            var Q40;
            {var subQ0=sQuery(id+"F1.wireOp",EDGE,"E84");var subQ1=sQuery(id+"F1.wireOp",EDGE,"E33.0");var subQ2=makeQuery(id+"F1.imprint","INTERSECT",VERTEX,{"derivedFrom":[subQ1,subQ0]});Q40=makeQuery(id+"F1.imprint","IMPRINT",FACE,{"disambiguationData":[TD([[makeQuery(id+"F1.imprint","IMPRINT",EDGE,{"disambiguationData":[TD([[subQ2,-1.0]])],"derivedFrom":subQ1}),-1.0]])]});}
            var Q41;
            {var subQ0=sQuery(id+"F1.wireOp",EDGE,"E146.trimOffspring");Q41=makeQuery(id+"F1.imprint","IMPRINT",FACE,{"disambiguationData":[TD([[makeQuery(id+"F1.imprint","IMPRINT",EDGE,{"derivedFrom":subQ0}),1.0]])]});}
            var Q42;
            {var subQ0=sQuery(id+"F1.wireOp",EDGE,"E95.trimOffspring");Q42=makeQuery(id+"F1.imprint","IMPRINT",FACE,{"disambiguationData":[TD([[makeQuery(id+"F1.imprint","IMPRINT",EDGE,{"derivedFrom":subQ0}),-1.0]])]});}
            var Q43;
            {var subQ0=sQuery(id+"F1.wireOp",EDGE,"E134.trimOffspring");Q43=makeQuery(id+"F1.imprint","IMPRINT",FACE,{"disambiguationData":[TD([[makeQuery(id+"F1.imprint","IMPRINT",EDGE,{"derivedFrom":subQ0}),1.0]])]});}
            var Q44;
            {var subQ0=sQuery(id+"F1.wireOp",EDGE,"E122.trimOffspring");Q44=makeQuery(id+"F1.imprint","IMPRINT",FACE,{"disambiguationData":[TD([[makeQuery(id+"F1.imprint","IMPRINT",EDGE,{"derivedFrom":subQ0}),-1.0]])]});}
            var Q45;
            {var subQ0=sQuery(id+"F1.wireOp",EDGE,"E105.trimOffspring");Q45=makeQuery(id+"F1.imprint","IMPRINT",FACE,{"disambiguationData":[TD([[makeQuery(id+"F1.imprint","IMPRINT",EDGE,{"derivedFrom":subQ0}),-1.0]])]});}
            var Q46;
            {var subQ0=sQuery(id+"F1.wireOp",EDGE,"E84");var subQ1=sQuery(id+"F1.wireOp",EDGE,"E31.0");var subQ2=makeQuery(id+"F1.imprint","INTERSECT",VERTEX,{"derivedFrom":[subQ1,subQ0]});Q46=makeQuery(id+"F1.imprint","IMPRINT",FACE,{"disambiguationData":[TD([[makeQuery(id+"F1.imprint","IMPRINT",EDGE,{"disambiguationData":[TD([[subQ2,-1.0]])],"derivedFrom":subQ1}),-1.0]])]});}
            var Q47;
            {var subQ0=sQuery(id+"F1.wireOp",EDGE,"E84");var subQ1=sQuery(id+"F1.wireOp",EDGE,"E24.0");var subQ2=makeQuery(id+"F1.imprint","INTERSECT",VERTEX,{"derivedFrom":[subQ1,subQ0]});Q47=makeQuery(id+"F1.imprint","IMPRINT",FACE,{"disambiguationData":[TD([[makeQuery(id+"F1.imprint","IMPRINT",EDGE,{"disambiguationData":[TD([[subQ2,-1.0]])],"derivedFrom":subQ1}),1.0]])]});}
            var Q48;
            {var subQ0=sQuery(id+"F1.wireOp",EDGE,"E84");var subQ1=sQuery(id+"F1.wireOp",EDGE,"E43.0");var subQ2=makeQuery(id+"F1.imprint","INTERSECT",VERTEX,{"derivedFrom":[subQ1,subQ0]});Q48=makeQuery(id+"F1.imprint","IMPRINT",FACE,{"disambiguationData":[TD([[makeQuery(id+"F1.imprint","IMPRINT",EDGE,{"disambiguationData":[TD([[subQ2,-1.0]])],"derivedFrom":subQ1}),1.0]])]});}
            var Q49;
            {var subQ0=sQuery(id+"F1.wireOp",EDGE,"E123.trimOffspring");Q49=makeQuery(id+"F1.imprint","IMPRINT",FACE,{"disambiguationData":[TD([[makeQuery(id+"F1.imprint","IMPRINT",EDGE,{"derivedFrom":subQ0}),-1.0]])]});}
            var Q50;
            {var subQ0=sQuery(id+"F1.wireOp",EDGE,"E84");var subQ1=sQuery(id+"F1.wireOp",EDGE,"E43.0");var subQ2=makeQuery(id+"F1.imprint","INTERSECT",VERTEX,{"derivedFrom":[subQ1,subQ0]});Q50=makeQuery(id+"F1.imprint","IMPRINT",FACE,{"disambiguationData":[TD([[makeQuery(id+"F1.imprint","IMPRINT",EDGE,{"disambiguationData":[TD([[subQ2,-1.0]])],"derivedFrom":subQ1}),-1.0]])]});}
            var Q51;
            {var subQ0=sQuery(id+"F1.wireOp",EDGE,"E84");var subQ1=sQuery(id+"F1.wireOp",EDGE,"E32.0");var subQ2=makeQuery(id+"F1.imprint","INTERSECT",VERTEX,{"derivedFrom":[subQ1,subQ0]});Q51=makeQuery(id+"F1.imprint","IMPRINT",FACE,{"disambiguationData":[TD([[makeQuery(id+"F1.imprint","IMPRINT",EDGE,{"disambiguationData":[TD([[subQ2,-1.0]])],"derivedFrom":subQ1}),1.0]])]});}
            var Q52;
            {var subQ0=sQuery(id+"F1.wireOp",EDGE,"E133.trimOffspring");Q52=makeQuery(id+"F1.imprint","IMPRINT",FACE,{"disambiguationData":[TD([[makeQuery(id+"F1.imprint","IMPRINT",EDGE,{"derivedFrom":subQ0}),1.0]])]});}
            var Q53;
            {var subQ0=sQuery(id+"F1.wireOp",EDGE,"E84");var subQ1=sQuery(id+"F1.wireOp",EDGE,"E37.0");var subQ2=makeQuery(id+"F1.imprint","INTERSECT",VERTEX,{"derivedFrom":[subQ1,subQ0]});Q53=makeQuery(id+"F1.imprint","IMPRINT",FACE,{"disambiguationData":[TD([[makeQuery(id+"F1.imprint","IMPRINT",EDGE,{"disambiguationData":[TD([[subQ2,-1.0]])],"derivedFrom":subQ1}),1.0]])]});}
            var Q54;
            {var subQ0=sQuery(id+"F1.wireOp",EDGE,"E141");Q54=makeQuery(id+"F1.imprint","IMPRINT",FACE,{"disambiguationData":[TD([[makeQuery(id+"F1.imprint","IMPRINT",EDGE,{"derivedFrom":subQ0}),1.0]])]});}
            var Q55;
            {var subQ0=sQuery(id+"F1.wireOp",EDGE,"E84");var subQ1=sQuery(id+"F1.wireOp",EDGE,"E17.0");var subQ2=makeQuery(id+"F1.imprint","INTERSECT",VERTEX,{"derivedFrom":[subQ1,subQ0]});Q55=makeQuery(id+"F1.imprint","IMPRINT",FACE,{"disambiguationData":[TD([[makeQuery(id+"F1.imprint","IMPRINT",EDGE,{"disambiguationData":[TD([[subQ2,-1.0]])],"derivedFrom":subQ1}),1.0]])]});}
            var Q56;
            {var subQ0=sQuery(id+"F1.wireOp",EDGE,"E127.trimOffspring");Q56=makeQuery(id+"F1.imprint","IMPRINT",FACE,{"disambiguationData":[TD([[makeQuery(id+"F1.imprint","IMPRINT",EDGE,{"derivedFrom":subQ0}),1.0]])]});}
            var Q57;
            {var subQ0=sQuery(id+"F1.wireOp",EDGE,"E84");var subQ1=sQuery(id+"F1.wireOp",EDGE,"E8.0");var subQ2=makeQuery(id+"F1.imprint","INTERSECT",VERTEX,{"derivedFrom":[subQ1,subQ0]});Q57=makeQuery(id+"F1.imprint","IMPRINT",FACE,{"disambiguationData":[TD([[makeQuery(id+"F1.imprint","IMPRINT",EDGE,{"disambiguationData":[TD([[subQ2,-1.0]])],"derivedFrom":subQ1}),-1.0]])]});}
            var Q58;
            {var subQ0=sQuery(id+"F1.wireOp",EDGE,"E84");var subQ1=sQuery(id+"F1.wireOp",EDGE,"E35.0");var subQ2=makeQuery(id+"F1.imprint","INTERSECT",VERTEX,{"derivedFrom":[subQ1,subQ0]});Q58=makeQuery(id+"F1.imprint","IMPRINT",FACE,{"disambiguationData":[TD([[makeQuery(id+"F1.imprint","IMPRINT",EDGE,{"disambiguationData":[TD([[subQ2,-1.0]])],"derivedFrom":subQ1}),1.0]])]});}
            var Q59;
            {var subQ0=sQuery(id+"F1.wireOp",EDGE,"E84");var subQ1=sQuery(id+"F1.wireOp",EDGE,"E27.0");var subQ2=makeQuery(id+"F1.imprint","INTERSECT",VERTEX,{"derivedFrom":[subQ1,subQ0]});Q59=makeQuery(id+"F1.imprint","IMPRINT",FACE,{"disambiguationData":[TD([[makeQuery(id+"F1.imprint","IMPRINT",EDGE,{"disambiguationData":[TD([[subQ2,-1.0]])],"derivedFrom":subQ1}),1.0]])]});}
            var Q60;
            {var subQ0=sQuery(id+"F1.wireOp",EDGE,"E84");var subQ1=sQuery(id+"F1.wireOp",EDGE,"E42.0");var subQ2=makeQuery(id+"F1.imprint","INTERSECT",VERTEX,{"derivedFrom":[subQ1,subQ0]});Q60=makeQuery(id+"F1.imprint","IMPRINT",FACE,{"disambiguationData":[TD([[makeQuery(id+"F1.imprint","IMPRINT",EDGE,{"disambiguationData":[TD([[subQ2,-1.0]])],"derivedFrom":subQ1}),-1.0]])]});}
            var Q61;
            {var subQ0=sQuery(id+"F1.wireOp",EDGE,"E93.trimOffspring");Q61=makeQuery(id+"F1.imprint","IMPRINT",FACE,{"disambiguationData":[TD([[makeQuery(id+"F1.imprint","IMPRINT",EDGE,{"derivedFrom":subQ0}),-1.0]])]});}
            var Q62;
            {var subQ0=sQuery(id+"F1.wireOp",EDGE,"E84");var subQ1=sQuery(id+"F1.wireOp",EDGE,"E28.0");var subQ2=makeQuery(id+"F1.imprint","INTERSECT",VERTEX,{"derivedFrom":[subQ1,subQ0]});Q62=makeQuery(id+"F1.imprint","IMPRINT",FACE,{"disambiguationData":[TD([[makeQuery(id+"F1.imprint","IMPRINT",EDGE,{"disambiguationData":[TD([[subQ2,-1.0]])],"derivedFrom":subQ1}),-1.0]])]});}
            var Q63;
            {var subQ0=sQuery(id+"F1.wireOp",EDGE,"E84");var subQ1=sQuery(id+"F1.wireOp",EDGE,"E12.0");var subQ2=makeQuery(id+"F1.imprint","INTERSECT",VERTEX,{"derivedFrom":[subQ1,subQ0]});Q63=makeQuery(id+"F1.imprint","IMPRINT",FACE,{"disambiguationData":[TD([[makeQuery(id+"F1.imprint","IMPRINT",EDGE,{"disambiguationData":[TD([[subQ2,-1.0]])],"derivedFrom":subQ1}),-1.0]])]});}
            var Q64;
            {var subQ0=sQuery(id+"F1.wireOp",EDGE,"E84");var subQ1=sQuery(id+"F1.wireOp",EDGE,"E26.0");var subQ2=makeQuery(id+"F1.imprint","INTERSECT",VERTEX,{"derivedFrom":[subQ1,subQ0]});Q64=makeQuery(id+"F1.imprint","IMPRINT",FACE,{"disambiguationData":[TD([[makeQuery(id+"F1.imprint","IMPRINT",EDGE,{"disambiguationData":[TD([[subQ2,-1.0]])],"derivedFrom":subQ1}),1.0]])]});}
            var Q65;
            {var subQ0=sQuery(id+"F1.wireOp",EDGE,"E148.trimOffspring");Q65=makeQuery(id+"F1.imprint","IMPRINT",FACE,{"disambiguationData":[TD([[makeQuery(id+"F1.imprint","IMPRINT",EDGE,{"derivedFrom":subQ0}),1.0]])]});}
            var Q66;
            {var subQ0=sQuery(id+"F1.wireOp",EDGE,"E142.trimOffspring");Q66=makeQuery(id+"F1.imprint","IMPRINT",FACE,{"disambiguationData":[TD([[makeQuery(id+"F1.imprint","IMPRINT",EDGE,{"derivedFrom":subQ0}),1.0]])]});}
            var Q67;
            {var subQ0=sQuery(id+"F1.wireOp",EDGE,"E106.trimOffspring");Q67=makeQuery(id+"F1.imprint","IMPRINT",FACE,{"disambiguationData":[TD([[makeQuery(id+"F1.imprint","IMPRINT",EDGE,{"derivedFrom":subQ0}),-1.0]])]});}
            var Q68;
            {var subQ0=sQuery(id+"F1.wireOp",EDGE,"E84");var subQ1=sQuery(id+"F1.wireOp",EDGE,"E28.0");var subQ2=makeQuery(id+"F1.imprint","INTERSECT",VERTEX,{"derivedFrom":[subQ1,subQ0]});Q68=makeQuery(id+"F1.imprint","IMPRINT",FACE,{"disambiguationData":[TD([[makeQuery(id+"F1.imprint","IMPRINT",EDGE,{"disambiguationData":[TD([[subQ2,-1.0]])],"derivedFrom":subQ1}),1.0]])]});}
            var Q69;
            {var subQ0=sQuery(id+"F1.wireOp",EDGE,"E92.trimOffspring");Q69=makeQuery(id+"F1.imprint","IMPRINT",FACE,{"disambiguationData":[TD([[makeQuery(id+"F1.imprint","IMPRINT",EDGE,{"derivedFrom":subQ0}),-1.0]])]});}
            var Q70;
            {var subQ0=sQuery(id+"F1.wireOp",EDGE,"E84");var subQ1=sQuery(id+"F1.wireOp",EDGE,"E7.0");var subQ2=makeQuery(id+"F1.imprint","INTERSECT",VERTEX,{"derivedFrom":[subQ1,subQ0]});Q70=makeQuery(id+"F1.imprint","IMPRINT",FACE,{"disambiguationData":[TD([[makeQuery(id+"F1.imprint","IMPRINT",EDGE,{"disambiguationData":[TD([[subQ2,-1.0]])],"derivedFrom":subQ1}),-1.0]])]});}
            var Q71;
            {var subQ0=sQuery(id+"F1.wireOp",EDGE,"E84");var subQ1=sQuery(id+"F1.wireOp",EDGE,"E31.0");var subQ2=makeQuery(id+"F1.imprint","INTERSECT",VERTEX,{"derivedFrom":[subQ1,subQ0]});Q71=makeQuery(id+"F1.imprint","IMPRINT",FACE,{"disambiguationData":[TD([[makeQuery(id+"F1.imprint","IMPRINT",EDGE,{"disambiguationData":[TD([[subQ2,-1.0]])],"derivedFrom":subQ1}),1.0]])]});}
            var Q72;
            {var subQ0=sQuery(id+"F1.wireOp",EDGE,"E152");Q72=makeQuery(id+"F1.imprint","IMPRINT",FACE,{"disambiguationData":[TD([[makeQuery(id+"F1.imprint","IMPRINT",EDGE,{"derivedFrom":subQ0}),1.0]])]});}
            var Q73;
            {var subQ0=sQuery(id+"F1.wireOp",EDGE,"E87.trimOffspring");Q73=makeQuery(id+"F1.imprint","IMPRINT",FACE,{"disambiguationData":[TD([[makeQuery(id+"F1.imprint","IMPRINT",EDGE,{"derivedFrom":subQ0}),-1.0]])]});}
            var Q74;
            {var subQ0=sQuery(id+"F1.wireOp",EDGE,"E84");var subQ1=sQuery(id+"F1.wireOp",EDGE,"E22.0");var subQ2=makeQuery(id+"F1.imprint","INTERSECT",VERTEX,{"derivedFrom":[subQ1,subQ0]});Q74=makeQuery(id+"F1.imprint","IMPRINT",FACE,{"disambiguationData":[TD([[makeQuery(id+"F1.imprint","IMPRINT",EDGE,{"disambiguationData":[TD([[subQ2,-1.0]])],"derivedFrom":subQ1}),-1.0]])]});}
            var Q75;
            {var subQ0=sQuery(id+"F1.wireOp",EDGE,"E84");var subQ1=sQuery(id+"F1.wireOp",EDGE,"E44.0");var subQ2=makeQuery(id+"F1.imprint","INTERSECT",VERTEX,{"derivedFrom":[subQ1,subQ0]});Q75=makeQuery(id+"F1.imprint","IMPRINT",FACE,{"disambiguationData":[TD([[makeQuery(id+"F1.imprint","IMPRINT",EDGE,{"disambiguationData":[TD([[subQ2,-1.0]])],"derivedFrom":subQ1}),1.0]])]});}
            var Q76;
            {var subQ0=sQuery(id+"F1.wireOp",EDGE,"E84");var subQ1=sQuery(id+"F1.wireOp",EDGE,"E18.0");var subQ2=makeQuery(id+"F1.imprint","INTERSECT",VERTEX,{"derivedFrom":[subQ1,subQ0]});Q76=makeQuery(id+"F1.imprint","IMPRINT",FACE,{"disambiguationData":[TD([[makeQuery(id+"F1.imprint","IMPRINT",EDGE,{"disambiguationData":[TD([[subQ2,-1.0]])],"derivedFrom":subQ1}),1.0]])]});}
            var Q77;
            {var subQ0=sQuery(id+"F1.wireOp",EDGE,"E96.trimOffspring");Q77=makeQuery(id+"F1.imprint","IMPRINT",FACE,{"disambiguationData":[TD([[makeQuery(id+"F1.imprint","IMPRINT",EDGE,{"derivedFrom":subQ0}),-1.0]])]});}
            var Q78;
            {var subQ0=sQuery(id+"F1.wireOp",EDGE,"E139.trimOffspring");Q78=makeQuery(id+"F1.imprint","IMPRINT",FACE,{"disambiguationData":[TD([[makeQuery(id+"F1.imprint","IMPRINT",EDGE,{"derivedFrom":subQ0}),1.0]])]});}
            var Q79;
            {var subQ0=sQuery(id+"F1.wireOp",EDGE,"E84");var subQ1=sQuery(id+"F1.wireOp",EDGE,"E7.0");var subQ2=makeQuery(id+"F1.imprint","INTERSECT",VERTEX,{"derivedFrom":[subQ1,subQ0]});Q79=makeQuery(id+"F1.imprint","IMPRINT",FACE,{"disambiguationData":[TD([[makeQuery(id+"F1.imprint","IMPRINT",EDGE,{"disambiguationData":[TD([[subQ2,-1.0]])],"derivedFrom":subQ1}),1.0]])]});}
            var Q80;
            {var subQ0=sQuery(id+"F1.wireOp",EDGE,"E84");var subQ1=sQuery(id+"F1.wireOp",EDGE,"E30.0");var subQ2=makeQuery(id+"F1.imprint","INTERSECT",VERTEX,{"derivedFrom":[subQ1,subQ0]});Q80=makeQuery(id+"F1.imprint","IMPRINT",FACE,{"disambiguationData":[TD([[makeQuery(id+"F1.imprint","IMPRINT",EDGE,{"disambiguationData":[TD([[subQ2,-1.0]])],"derivedFrom":subQ1}),1.0]])]});}
            var Q81;
            {var subQ0=sQuery(id+"F1.wireOp",EDGE,"E125.trimOffspring");Q81=makeQuery(id+"F1.imprint","IMPRINT",FACE,{"disambiguationData":[TD([[makeQuery(id+"F1.imprint","IMPRINT",EDGE,{"derivedFrom":subQ0}),1.0]])]});}
            var Q82;
            {var subQ0=sQuery(id+"F1.wireOp",EDGE,"E124.trimOffspring");Q82=makeQuery(id+"F1.imprint","IMPRINT",FACE,{"disambiguationData":[TD([[makeQuery(id+"F1.imprint","IMPRINT",EDGE,{"derivedFrom":subQ0}),-1.0]])]});}
            var Q83;
            {var subQ0=sQuery(id+"F1.wireOp",EDGE,"E84");var subQ1=sQuery(id+"F1.wireOp",EDGE,"E27.0");var subQ2=makeQuery(id+"F1.imprint","INTERSECT",VERTEX,{"derivedFrom":[subQ1,subQ0]});Q83=makeQuery(id+"F1.imprint","IMPRINT",FACE,{"disambiguationData":[TD([[makeQuery(id+"F1.imprint","IMPRINT",EDGE,{"disambiguationData":[TD([[subQ2,-1.0]])],"derivedFrom":subQ1}),-1.0]])]});}
            var Q84;
            {var subQ0=sQuery(id+"F1.wireOp",EDGE,"E147.trimOffspring");Q84=makeQuery(id+"F1.imprint","IMPRINT",FACE,{"disambiguationData":[TD([[makeQuery(id+"F1.imprint","IMPRINT",EDGE,{"derivedFrom":subQ0}),1.0]])]});}
            var Q85;
            {var subQ0=sQuery(id+"F1.wireOp",EDGE,"E84");var subQ1=sQuery(id+"F1.wireOp",EDGE,"E37.0");var subQ2=makeQuery(id+"F1.imprint","INTERSECT",VERTEX,{"derivedFrom":[subQ1,subQ0]});Q85=makeQuery(id+"F1.imprint","IMPRINT",FACE,{"disambiguationData":[TD([[makeQuery(id+"F1.imprint","IMPRINT",EDGE,{"disambiguationData":[TD([[subQ2,-1.0]])],"derivedFrom":subQ1}),-1.0]])]});}
            var Q86;
            {var subQ0=sQuery(id+"F1.wireOp",EDGE,"E84");var subQ1=sQuery(id+"F1.wireOp",EDGE,"E32.0");var subQ2=makeQuery(id+"F1.imprint","INTERSECT",VERTEX,{"derivedFrom":[subQ1,subQ0]});Q86=makeQuery(id+"F1.imprint","IMPRINT",FACE,{"disambiguationData":[TD([[makeQuery(id+"F1.imprint","IMPRINT",EDGE,{"disambiguationData":[TD([[subQ2,-1.0]])],"derivedFrom":subQ1}),-1.0]])]});}
            var Q87;
            {var subQ0=sQuery(id+"F1.wireOp",EDGE,"E131");Q87=makeQuery(id+"F1.imprint","IMPRINT",FACE,{"disambiguationData":[TD([[makeQuery(id+"F1.imprint","IMPRINT",EDGE,{"derivedFrom":subQ0}),1.0]])]});}
            var Q88;
            {var subQ0=sQuery(id+"F1.wireOp",EDGE,"E84");var subQ1=sQuery(id+"F1.wireOp",EDGE,"E34.0");var subQ2=makeQuery(id+"F1.imprint","INTERSECT",VERTEX,{"derivedFrom":[subQ1,subQ0]});Q88=makeQuery(id+"F1.imprint","IMPRINT",FACE,{"disambiguationData":[TD([[makeQuery(id+"F1.imprint","IMPRINT",EDGE,{"disambiguationData":[TD([[subQ2,-1.0]])],"derivedFrom":subQ1}),-1.0]])]});}
            var Q89;
            {var subQ0=sQuery(id+"F1.wireOp",EDGE,"E84");var subQ1=sQuery(id+"F1.wireOp",EDGE,"E14.0");var subQ2=makeQuery(id+"F1.imprint","INTERSECT",VERTEX,{"derivedFrom":[subQ1,subQ0]});Q89=makeQuery(id+"F1.imprint","IMPRINT",FACE,{"disambiguationData":[TD([[makeQuery(id+"F1.imprint","IMPRINT",EDGE,{"disambiguationData":[TD([[subQ2,-1.0]])],"derivedFrom":subQ1}),1.0]])]});}
            var Q90;
            {var subQ0=sQuery(id+"F1.wireOp",EDGE,"E145.trimOffspring");Q90=makeQuery(id+"F1.imprint","IMPRINT",FACE,{"disambiguationData":[TD([[makeQuery(id+"F1.imprint","IMPRINT",EDGE,{"derivedFrom":subQ0}),1.0]])]});}
            var Q91;
            {var subQ0=sQuery(id+"F1.wireOp",EDGE,"E84");var subQ1=sQuery(id+"F1.wireOp",EDGE,"E44.0");var subQ2=makeQuery(id+"F1.imprint","INTERSECT",VERTEX,{"derivedFrom":[subQ1,subQ0]});Q91=makeQuery(id+"F1.imprint","IMPRINT",FACE,{"disambiguationData":[TD([[makeQuery(id+"F1.imprint","IMPRINT",EDGE,{"disambiguationData":[TD([[subQ2,-1.0]])],"derivedFrom":subQ1}),-1.0]])]});}
            var Q92;
            {var subQ0=sQuery(id+"F1.wireOp",EDGE,"E101.trimOffspring");Q92=makeQuery(id+"F1.imprint","IMPRINT",FACE,{"disambiguationData":[TD([[makeQuery(id+"F1.imprint","IMPRINT",EDGE,{"derivedFrom":subQ0}),-1.0]])]});}
            var Q93;
            {var subQ0=sQuery(id+"F1.wireOp",EDGE,"E84");var subQ1=sQuery(id+"F1.wireOp",EDGE,"E20.0");var subQ2=makeQuery(id+"F1.imprint","INTERSECT",VERTEX,{"derivedFrom":[subQ1,subQ0]});Q93=makeQuery(id+"F1.imprint","IMPRINT",FACE,{"disambiguationData":[TD([[makeQuery(id+"F1.imprint","IMPRINT",EDGE,{"disambiguationData":[TD([[subQ2,-1.0]])],"derivedFrom":subQ1}),-1.0]])]});}
            var Q94;
            {var subQ0=sQuery(id+"F1.wireOp",EDGE,"E89.trimOffspring");Q94=makeQuery(id+"F1.imprint","IMPRINT",FACE,{"disambiguationData":[TD([[makeQuery(id+"F1.imprint","IMPRINT",EDGE,{"derivedFrom":subQ0}),-1.0]])]});}
            var Q95;
            {var subQ0=sQuery(id+"F1.wireOp",EDGE,"E84");var subQ1=sQuery(id+"F1.wireOp",EDGE,"E36.0");var subQ2=makeQuery(id+"F1.imprint","INTERSECT",VERTEX,{"derivedFrom":[subQ1,subQ0]});Q95=makeQuery(id+"F1.imprint","IMPRINT",FACE,{"disambiguationData":[TD([[makeQuery(id+"F1.imprint","IMPRINT",EDGE,{"disambiguationData":[TD([[subQ2,-1.0]])],"derivedFrom":subQ1}),-1.0]])]});}
            var Q96;
            {var subQ0=sQuery(id+"F1.wireOp",EDGE,"E150.trimOffspring");Q96=makeQuery(id+"F1.imprint","IMPRINT",FACE,{"disambiguationData":[TD([[makeQuery(id+"F1.imprint","IMPRINT",EDGE,{"derivedFrom":subQ0}),1.0]])]});}
            var Q97;
            {var subQ0=sQuery(id+"F1.wireOp",EDGE,"E84");var subQ1=sQuery(id+"F1.wireOp",EDGE,"E34.0");var subQ2=makeQuery(id+"F1.imprint","INTERSECT",VERTEX,{"derivedFrom":[subQ1,subQ0]});Q97=makeQuery(id+"F1.imprint","IMPRINT",FACE,{"disambiguationData":[TD([[makeQuery(id+"F1.imprint","IMPRINT",EDGE,{"disambiguationData":[TD([[subQ2,-1.0]])],"derivedFrom":subQ1}),1.0]])]});}
            var Q98;
            {var subQ0=sQuery(id+"F1.wireOp",EDGE,"E103.trimOffspring");Q98=makeQuery(id+"F1.imprint","IMPRINT",FACE,{"disambiguationData":[TD([[makeQuery(id+"F1.imprint","IMPRINT",EDGE,{"derivedFrom":subQ0}),-1.0]])]});}
            var Q99;
            {var subQ0=sQuery(id+"F1.wireOp",EDGE,"E84");var subQ1=sQuery(id+"F1.wireOp",EDGE,"E16.0");var subQ2=makeQuery(id+"F1.imprint","INTERSECT",VERTEX,{"derivedFrom":[subQ1,subQ0]});Q99=makeQuery(id+"F1.imprint","IMPRINT",FACE,{"disambiguationData":[TD([[makeQuery(id+"F1.imprint","IMPRINT",EDGE,{"disambiguationData":[TD([[subQ2,-1.0]])],"derivedFrom":subQ1}),-1.0]])]});}
            var Q100;
            {var subQ0=sQuery(id+"F1.wireOp",EDGE,"E109.trimOffspring");Q100=makeQuery(id+"F1.imprint","IMPRINT",FACE,{"disambiguationData":[TD([[makeQuery(id+"F1.imprint","IMPRINT",EDGE,{"derivedFrom":subQ0}),-1.0]])]});}
            var Q101;
            {var subQ0=sQuery(id+"F1.wireOp",EDGE,"E155.trimOffspring");Q101=makeQuery(id+"F1.imprint","IMPRINT",FACE,{"disambiguationData":[TD([[makeQuery(id+"F1.imprint","IMPRINT",EDGE,{"derivedFrom":subQ0}),1.0]])]});}
            var Q102;
            {var subQ0=sQuery(id+"F1.wireOp",EDGE,"E90.trimOffspring");Q102=makeQuery(id+"F1.imprint","IMPRINT",FACE,{"disambiguationData":[TD([[makeQuery(id+"F1.imprint","IMPRINT",EDGE,{"derivedFrom":subQ0}),-1.0]])]});}
            var Q103;
            {var subQ0=sQuery(id+"F1.wireOp",EDGE,"E128.trimOffspring");Q103=makeQuery(id+"F1.imprint","IMPRINT",FACE,{"disambiguationData":[TD([[makeQuery(id+"F1.imprint","IMPRINT",EDGE,{"derivedFrom":subQ0}),1.0]])]});}
            var Q104;
            {var subQ0=sQuery(id+"F1.wireOp",EDGE,"E84");var subQ1=sQuery(id+"F1.wireOp",EDGE,"E23.0");var subQ2=makeQuery(id+"F1.imprint","INTERSECT",VERTEX,{"derivedFrom":[subQ1,subQ0]});Q104=makeQuery(id+"F1.imprint","IMPRINT",FACE,{"disambiguationData":[TD([[makeQuery(id+"F1.imprint","IMPRINT",EDGE,{"disambiguationData":[TD([[subQ2,-1.0]])],"derivedFrom":subQ1}),-1.0]])]});}
            var Q105;
            {var subQ0=sQuery(id+"F1.wireOp",EDGE,"E84");var subQ1=sQuery(id+"F1.wireOp",EDGE,"E42.0");var subQ2=makeQuery(id+"F1.imprint","INTERSECT",VERTEX,{"derivedFrom":[subQ1,subQ0]});Q105=makeQuery(id+"F1.imprint","IMPRINT",FACE,{"disambiguationData":[TD([[makeQuery(id+"F1.imprint","IMPRINT",EDGE,{"disambiguationData":[TD([[subQ2,-1.0]])],"derivedFrom":subQ1}),1.0]])]});}
            var Q106;
            {var subQ0=sQuery(id+"F1.wireOp",EDGE,"E108.trimOffspring");Q106=makeQuery(id+"F1.imprint","IMPRINT",FACE,{"disambiguationData":[TD([[makeQuery(id+"F1.imprint","IMPRINT",EDGE,{"derivedFrom":subQ0}),-1.0]])]});}
            var Q107;
            {var subQ0=sQuery(id+"F1.wireOp",EDGE,"E84");var subQ1=sQuery(id+"F1.wireOp",EDGE,"E29.0");var subQ2=makeQuery(id+"F1.imprint","INTERSECT",VERTEX,{"derivedFrom":[subQ1,subQ0]});Q107=makeQuery(id+"F1.imprint","IMPRINT",FACE,{"disambiguationData":[TD([[makeQuery(id+"F1.imprint","IMPRINT",EDGE,{"disambiguationData":[TD([[subQ2,-1.0]])],"derivedFrom":subQ1}),1.0]])]});}
            var Q108;
            {var subQ0=sQuery(id+"F1.wireOp",EDGE,"E110.trimOffspring");Q108=makeQuery(id+"F1.imprint","IMPRINT",FACE,{"disambiguationData":[TD([[makeQuery(id+"F1.imprint","IMPRINT",EDGE,{"derivedFrom":subQ0}),-1.0]])]});}
            var Q109;
            {var subQ0=sQuery(id+"F1.wireOp",EDGE,"E159");Q109=makeQuery(id+"F1.imprint","IMPRINT",FACE,{"disambiguationData":[TD([[makeQuery(id+"F1.imprint","IMPRINT",EDGE,{"derivedFrom":subQ0}),1.0]])]});}
            var Q110;
            {var subQ0=sQuery(id+"F1.wireOp",EDGE,"E119.trimOffspring");Q110=makeQuery(id+"F1.imprint","IMPRINT",FACE,{"disambiguationData":[TD([[makeQuery(id+"F1.imprint","IMPRINT",EDGE,{"derivedFrom":subQ0}),-1.0]])]});}
            var Q111;
            {var subQ0=sQuery(id+"F1.wireOp",EDGE,"E84");var subQ1=sQuery(id+"F1.wireOp",EDGE,"E24.0");var subQ2=makeQuery(id+"F1.imprint","INTERSECT",VERTEX,{"derivedFrom":[subQ1,subQ0]});Q111=makeQuery(id+"F1.imprint","IMPRINT",FACE,{"disambiguationData":[TD([[makeQuery(id+"F1.imprint","IMPRINT",EDGE,{"disambiguationData":[TD([[subQ2,-1.0]])],"derivedFrom":subQ1}),-1.0]])]});}
            var Q112;
            {var subQ0=sQuery(id+"F1.wireOp",EDGE,"E97.trimOffspring");Q112=makeQuery(id+"F1.imprint","IMPRINT",FACE,{"disambiguationData":[TD([[makeQuery(id+"F1.imprint","IMPRINT",EDGE,{"derivedFrom":subQ0}),-1.0]])]});}
            var Q113;
            {var subQ0=sQuery(id+"F1.wireOp",EDGE,"E84");var subQ1=sQuery(id+"F1.wireOp",EDGE,"E23.0");var subQ2=makeQuery(id+"F1.imprint","INTERSECT",VERTEX,{"derivedFrom":[subQ1,subQ0]});Q113=makeQuery(id+"F1.imprint","IMPRINT",FACE,{"disambiguationData":[TD([[makeQuery(id+"F1.imprint","IMPRINT",EDGE,{"disambiguationData":[TD([[subQ2,-1.0]])],"derivedFrom":subQ1}),1.0]])]});}
            var Q114;
            {var subQ0=sQuery(id+"F1.wireOp",EDGE,"E132");Q114=makeQuery(id+"F1.imprint","IMPRINT",FACE,{"disambiguationData":[TD([[makeQuery(id+"F1.imprint","IMPRINT",EDGE,{"derivedFrom":subQ0}),1.0]])]});}
            var Q115;
            {var subQ0=sQuery(id+"F1.wireOp",EDGE,"E84");var subQ1=sQuery(id+"F1.wireOp",EDGE,"E8.0");var subQ2=makeQuery(id+"F1.imprint","INTERSECT",VERTEX,{"derivedFrom":[subQ1,subQ0]});Q115=makeQuery(id+"F1.imprint","IMPRINT",FACE,{"disambiguationData":[TD([[makeQuery(id+"F1.imprint","IMPRINT",EDGE,{"disambiguationData":[TD([[subQ2,-1.0]])],"derivedFrom":subQ1}),1.0]])]});}
            var Q116;
            {var subQ0=sQuery(id+"F1.wireOp",EDGE,"E84");var subQ1=sQuery(id+"F1.wireOp",EDGE,"E16.0");var subQ2=makeQuery(id+"F1.imprint","INTERSECT",VERTEX,{"derivedFrom":[subQ1,subQ0]});Q116=makeQuery(id+"F1.imprint","IMPRINT",FACE,{"disambiguationData":[TD([[makeQuery(id+"F1.imprint","IMPRINT",EDGE,{"disambiguationData":[TD([[subQ2,-1.0]])],"derivedFrom":subQ1}),1.0]])]});}
            var Q117;
            {var subQ0=sQuery(id+"F1.wireOp",EDGE,"E84");var subQ1=sQuery(id+"F1.wireOp",EDGE,"E15.0");var subQ2=makeQuery(id+"F1.imprint","INTERSECT",VERTEX,{"derivedFrom":[subQ1,subQ0]});Q117=makeQuery(id+"F1.imprint","IMPRINT",FACE,{"disambiguationData":[TD([[makeQuery(id+"F1.imprint","IMPRINT",EDGE,{"disambiguationData":[TD([[subQ2,-1.0]])],"derivedFrom":subQ1}),1.0]])]});}
            var Q118;
            {var subQ0=sQuery(id+"F1.wireOp",EDGE,"E84");var subQ1=sQuery(id+"F1.wireOp",EDGE,"E41.0");var subQ2=makeQuery(id+"F1.imprint","INTERSECT",VERTEX,{"derivedFrom":[subQ1,subQ0]});Q118=makeQuery(id+"F1.imprint","IMPRINT",FACE,{"disambiguationData":[TD([[makeQuery(id+"F1.imprint","IMPRINT",EDGE,{"disambiguationData":[TD([[subQ2,-1.0]])],"derivedFrom":subQ1}),-1.0]])]});}
            var Q119;
            {var subQ0=sQuery(id+"F1.wireOp",EDGE,"E157.trimOffspring");Q119=makeQuery(id+"F1.imprint","IMPRINT",FACE,{"disambiguationData":[TD([[makeQuery(id+"F1.imprint","IMPRINT",EDGE,{"derivedFrom":subQ0}),1.0]])]});}
            var Q120;
            {var subQ0=sQuery(id+"F1.wireOp",EDGE,"E84");var subQ1=sQuery(id+"F1.wireOp",EDGE,"E6.0");var subQ2=makeQuery(id+"F1.imprint","INTERSECT",VERTEX,{"derivedFrom":[subQ1,subQ0]});Q120=makeQuery(id+"F1.imprint","IMPRINT",FACE,{"disambiguationData":[TD([[makeQuery(id+"F1.imprint","IMPRINT",EDGE,{"disambiguationData":[TD([[subQ2,-1.0]])],"derivedFrom":subQ1}),1.0]])]});}
            var Q121;
            {var subQ0=sQuery(id+"F1.wireOp",EDGE,"E104.trimOffspring");Q121=makeQuery(id+"F1.imprint","IMPRINT",FACE,{"disambiguationData":[TD([[makeQuery(id+"F1.imprint","IMPRINT",EDGE,{"derivedFrom":subQ0}),-1.0]])]});}
            var Q122;
            {var subQ0=sQuery(id+"F1.wireOp",EDGE,"E94.trimOffspring");Q122=makeQuery(id+"F1.imprint","IMPRINT",FACE,{"disambiguationData":[TD([[makeQuery(id+"F1.imprint","IMPRINT",EDGE,{"derivedFrom":subQ0}),-1.0]])]});}
            var Q123;
            {var subQ0=sQuery(id+"F1.wireOp",EDGE,"E84");var subQ1=sQuery(id+"F1.wireOp",EDGE,"E11.0");var subQ2=makeQuery(id+"F1.imprint","INTERSECT",VERTEX,{"derivedFrom":[subQ1,subQ0]});Q123=makeQuery(id+"F1.imprint","IMPRINT",FACE,{"disambiguationData":[TD([[makeQuery(id+"F1.imprint","IMPRINT",EDGE,{"disambiguationData":[TD([[subQ2,-1.0]])],"derivedFrom":subQ1}),-1.0]])]});}
            var Q124;
            {var subQ0=sQuery(id+"F1.wireOp",EDGE,"E84");var subQ1=sQuery(id+"F1.wireOp",EDGE,"E38.0");var subQ2=makeQuery(id+"F1.imprint","INTERSECT",VERTEX,{"derivedFrom":[subQ1,subQ0]});Q124=makeQuery(id+"F1.imprint","IMPRINT",FACE,{"disambiguationData":[TD([[makeQuery(id+"F1.imprint","IMPRINT",EDGE,{"disambiguationData":[TD([[subQ2,-1.0]])],"derivedFrom":subQ1}),-1.0]])]});}
            var Q125;
            {var subQ0=sQuery(id+"F1.wireOp",EDGE,"E84");var subQ1=sQuery(id+"F1.wireOp",EDGE,"E10.0");var subQ2=makeQuery(id+"F1.imprint","INTERSECT",VERTEX,{"derivedFrom":[subQ1,subQ0]});Q125=makeQuery(id+"F1.imprint","IMPRINT",FACE,{"disambiguationData":[TD([[makeQuery(id+"F1.imprint","IMPRINT",EDGE,{"disambiguationData":[TD([[subQ2,-1.0]])],"derivedFrom":subQ1}),1.0]])]});}
            var Q126;
            {var subQ0=sQuery(id+"F1.wireOp",EDGE,"E111.trimOffspring");Q126=makeQuery(id+"F1.imprint","IMPRINT",FACE,{"disambiguationData":[TD([[makeQuery(id+"F1.imprint","IMPRINT",EDGE,{"derivedFrom":subQ0}),-1.0]])]});}
            var Q127;
            {var subQ0=sQuery(id+"F1.wireOp",EDGE,"E144.trimOffspring");Q127=makeQuery(id+"F1.imprint","IMPRINT",FACE,{"disambiguationData":[TD([[makeQuery(id+"F1.imprint","IMPRINT",EDGE,{"derivedFrom":subQ0}),1.0]])]});}
            var Q128;
            {var subQ0=sQuery(id+"F1.wireOp",EDGE,"E135.trimOffspring");Q128=makeQuery(id+"F1.imprint","IMPRINT",FACE,{"disambiguationData":[TD([[makeQuery(id+"F1.imprint","IMPRINT",EDGE,{"derivedFrom":subQ0}),1.0]])]});}
            var Q129;
            {var subQ0=sQuery(id+"F1.wireOp",EDGE,"E84");var subQ1=sQuery(id+"F1.wireOp",EDGE,"E13.0");var subQ2=makeQuery(id+"F1.imprint","INTERSECT",VERTEX,{"derivedFrom":[subQ1,subQ0]});Q129=makeQuery(id+"F1.imprint","IMPRINT",FACE,{"disambiguationData":[TD([[makeQuery(id+"F1.imprint","IMPRINT",EDGE,{"disambiguationData":[TD([[subQ2,-1.0]])],"derivedFrom":subQ1}),1.0]])]});}
            var Q130;
            {var subQ0=sQuery(id+"F1.wireOp",EDGE,"E84");var subQ1=sQuery(id+"F1.wireOp",EDGE,"E25.0");var subQ2=makeQuery(id+"F1.imprint","INTERSECT",VERTEX,{"derivedFrom":[subQ1,subQ0]});Q130=makeQuery(id+"F1.imprint","IMPRINT",FACE,{"disambiguationData":[TD([[makeQuery(id+"F1.imprint","IMPRINT",EDGE,{"disambiguationData":[TD([[subQ2,-1.0]])],"derivedFrom":subQ1}),1.0]])]});}
            var Q131;
            {var subQ0=sQuery(id+"F1.wireOp",EDGE,"E162");Q131=makeQuery(id+"F1.imprint","IMPRINT",FACE,{"disambiguationData":[TD([[makeQuery(id+"F1.imprint","IMPRINT",EDGE,{"derivedFrom":subQ0}),1.0]])]});}
            var Q132;
            {var subQ0=sQuery(id+"F1.wireOp",EDGE,"E137");Q132=makeQuery(id+"F1.imprint","IMPRINT",FACE,{"disambiguationData":[TD([[makeQuery(id+"F1.imprint","IMPRINT",EDGE,{"derivedFrom":subQ0}),1.0]])]});}
            var Q133;
            {var subQ0=sQuery(id+"F1.wireOp",EDGE,"E116.trimOffspring");Q133=makeQuery(id+"F1.imprint","IMPRINT",FACE,{"disambiguationData":[TD([[makeQuery(id+"F1.imprint","IMPRINT",EDGE,{"derivedFrom":subQ0}),-1.0]])]});}
            var Q134;
            {var subQ0=sQuery(id+"F1.wireOp",EDGE,"E126.trimOffspring");Q134=makeQuery(id+"F1.imprint","IMPRINT",FACE,{"disambiguationData":[TD([[makeQuery(id+"F1.imprint","IMPRINT",EDGE,{"derivedFrom":subQ0}),1.0]])]});}
            var Q135;
            {var subQ0=sQuery(id+"F1.wireOp",EDGE,"E84");var subQ1=sQuery(id+"F1.wireOp",EDGE,"E9.0");var subQ2=makeQuery(id+"F1.imprint","INTERSECT",VERTEX,{"derivedFrom":[subQ1,subQ0]});Q135=makeQuery(id+"F1.imprint","IMPRINT",FACE,{"disambiguationData":[TD([[makeQuery(id+"F1.imprint","IMPRINT",EDGE,{"disambiguationData":[TD([[subQ2,-1.0]])],"derivedFrom":subQ1}),1.0]])]});}
            var Q136;
            {var subQ0=sQuery(id+"F1.wireOp",EDGE,"E84");var subQ1=sQuery(id+"F1.wireOp",EDGE,"E40.0");var subQ2=makeQuery(id+"F1.imprint","INTERSECT",VERTEX,{"derivedFrom":[subQ1,subQ0]});Q136=makeQuery(id+"F1.imprint","IMPRINT",FACE,{"disambiguationData":[TD([[makeQuery(id+"F1.imprint","IMPRINT",EDGE,{"disambiguationData":[TD([[subQ2,-1.0]])],"derivedFrom":subQ1}),-1.0]])]});}
            var Q137;
            {var subQ0=sQuery(id+"F1.wireOp",EDGE,"E149.trimOffspring");Q137=makeQuery(id+"F1.imprint","IMPRINT",FACE,{"disambiguationData":[TD([[makeQuery(id+"F1.imprint","IMPRINT",EDGE,{"derivedFrom":subQ0}),1.0]])]});}
            var Q138;
            {var subQ0=sQuery(id+"F1.wireOp",EDGE,"E84");var subQ1=sQuery(id+"F1.wireOp",EDGE,"E25.0");var subQ2=makeQuery(id+"F1.imprint","INTERSECT",VERTEX,{"derivedFrom":[subQ1,subQ0]});Q138=makeQuery(id+"F1.imprint","IMPRINT",FACE,{"disambiguationData":[TD([[makeQuery(id+"F1.imprint","IMPRINT",EDGE,{"disambiguationData":[TD([[subQ2,-1.0]])],"derivedFrom":subQ1}),-1.0]])]});}
            var Q139;
            {var subQ0=sQuery(id+"F1.wireOp",EDGE,"E84");var subQ1=sQuery(id+"F1.wireOp",EDGE,"E41.0");var subQ2=makeQuery(id+"F1.imprint","INTERSECT",VERTEX,{"derivedFrom":[subQ1,subQ0]});Q139=makeQuery(id+"F1.imprint","IMPRINT",FACE,{"disambiguationData":[TD([[makeQuery(id+"F1.imprint","IMPRINT",EDGE,{"disambiguationData":[TD([[subQ2,-1.0]])],"derivedFrom":subQ1}),1.0]])]});}
            var Q140;
            {var subQ0=sQuery(id+"F1.wireOp",EDGE,"E84");var subQ1=sQuery(id+"F1.wireOp",EDGE,"E45.0");var subQ2=makeQuery(id+"F1.imprint","INTERSECT",VERTEX,{"derivedFrom":[subQ1,subQ0]});Q140=makeQuery(id+"F1.imprint","IMPRINT",FACE,{"disambiguationData":[TD([[makeQuery(id+"F1.imprint","IMPRINT",EDGE,{"disambiguationData":[TD([[subQ2,-1.0]])],"derivedFrom":subQ1}),-1.0]])]});}
            var Q141;
            {var subQ0=sQuery(id+"F1.wireOp",EDGE,"E98.trimOffspring");Q141=makeQuery(id+"F1.imprint","IMPRINT",FACE,{"disambiguationData":[TD([[makeQuery(id+"F1.imprint","IMPRINT",EDGE,{"derivedFrom":subQ0}),-1.0]])]});}
            var Q142;
            {var subQ0=sQuery(id+"F1.wireOp",EDGE,"E163");Q142=makeQuery(id+"F1.imprint","IMPRINT",FACE,{"disambiguationData":[TD([[makeQuery(id+"F1.imprint","IMPRINT",EDGE,{"derivedFrom":subQ0}),1.0]])]});}
            var Q143;
            {var subQ0=sQuery(id+"F1.wireOp",EDGE,"E153");Q143=makeQuery(id+"F1.imprint","IMPRINT",FACE,{"disambiguationData":[TD([[makeQuery(id+"F1.imprint","IMPRINT",EDGE,{"derivedFrom":subQ0}),1.0]])]});}
            var Q144;
            {var subQ0=sQuery(id+"F1.wireOp",EDGE,"E113.trimOffspring");Q144=makeQuery(id+"F1.imprint","IMPRINT",FACE,{"disambiguationData":[TD([[makeQuery(id+"F1.imprint","IMPRINT",EDGE,{"derivedFrom":subQ0}),-1.0]])]});}
            var Q145;
            {var subQ0=sQuery(id+"F1.wireOp",EDGE,"E84");var subQ1=sQuery(id+"F1.wireOp",EDGE,"E22.0");var subQ2=makeQuery(id+"F1.imprint","INTERSECT",VERTEX,{"derivedFrom":[subQ1,subQ0]});Q145=makeQuery(id+"F1.imprint","IMPRINT",FACE,{"disambiguationData":[TD([[makeQuery(id+"F1.imprint","IMPRINT",EDGE,{"disambiguationData":[TD([[subQ2,-1.0]])],"derivedFrom":subQ1}),1.0]])]});}
            var Q146;
            {var subQ0=sQuery(id+"F1.wireOp",EDGE,"E84");var subQ1=sQuery(id+"F1.wireOp",EDGE,"E39.0");var subQ2=makeQuery(id+"F1.imprint","INTERSECT",VERTEX,{"derivedFrom":[subQ1,subQ0]});Q146=makeQuery(id+"F1.imprint","IMPRINT",FACE,{"disambiguationData":[TD([[makeQuery(id+"F1.imprint","IMPRINT",EDGE,{"disambiguationData":[TD([[subQ2,-1.0]])],"derivedFrom":subQ1}),-1.0]])]});}
            var Q147;
            {var subQ0=sQuery(id+"F1.wireOp",EDGE,"E84");var subQ1=sQuery(id+"F1.wireOp",EDGE,"E33.0");var subQ2=makeQuery(id+"F1.imprint","INTERSECT",VERTEX,{"derivedFrom":[subQ1,subQ0]});Q147=makeQuery(id+"F1.imprint","IMPRINT",FACE,{"disambiguationData":[TD([[makeQuery(id+"F1.imprint","IMPRINT",EDGE,{"disambiguationData":[TD([[subQ2,-1.0]])],"derivedFrom":subQ1}),1.0]])]});}
            var Q148;
            {var subQ0=sQuery(id+"F1.wireOp",EDGE,"E84");var subQ1=sQuery(id+"F1.wireOp",EDGE,"E5.0");var subQ2=makeQuery(id+"F1.imprint","INTERSECT",VERTEX,{"derivedFrom":[subQ1,subQ0]});Q148=makeQuery(id+"F1.imprint","IMPRINT",FACE,{"disambiguationData":[TD([[makeQuery(id+"F1.imprint","IMPRINT",EDGE,{"disambiguationData":[TD([[subQ2,-1.0]])],"derivedFrom":subQ1}),1.0]])]});}
            var Q149;
            {var subQ0=sQuery(id+"F1.wireOp",EDGE,"E160");Q149=makeQuery(id+"F1.imprint","IMPRINT",FACE,{"disambiguationData":[TD([[makeQuery(id+"F1.imprint","IMPRINT",EDGE,{"derivedFrom":subQ0}),1.0]])]});}
            var Q150;
            {var subQ0=sQuery(id+"F1.wireOp",EDGE,"E84");var subQ1=sQuery(id+"F1.wireOp",EDGE,"E20.0");var subQ2=makeQuery(id+"F1.imprint","INTERSECT",VERTEX,{"derivedFrom":[subQ1,subQ0]});Q150=makeQuery(id+"F1.imprint","IMPRINT",FACE,{"disambiguationData":[TD([[makeQuery(id+"F1.imprint","IMPRINT",EDGE,{"disambiguationData":[TD([[subQ2,-1.0]])],"derivedFrom":subQ1}),1.0]])]});}
            var Q151;
            {var subQ0=sQuery(id+"F1.wireOp",EDGE,"E114.trimOffspring");Q151=makeQuery(id+"F1.imprint","IMPRINT",FACE,{"disambiguationData":[TD([[makeQuery(id+"F1.imprint","IMPRINT",EDGE,{"derivedFrom":subQ0}),-1.0]])]});}
            var Q152;
            {var subQ0=sQuery(id+"F1.wireOp",EDGE,"E136.trimOffspring");Q152=makeQuery(id+"F1.imprint","IMPRINT",FACE,{"disambiguationData":[TD([[makeQuery(id+"F1.imprint","IMPRINT",EDGE,{"derivedFrom":subQ0}),1.0]])]});}
            var Q153;
            {var subQ0=sQuery(id+"F1.wireOp",EDGE,"E84");var subQ1=sQuery(id+"F1.wireOp",EDGE,"E4");var subQ2=makeQuery(id+"F1.imprint","INTERSECT",VERTEX,{"derivedFrom":[subQ1,subQ0]});Q153=makeQuery(id+"F1.imprint","IMPRINT",FACE,{"disambiguationData":[TD([[makeQuery(id+"F1.imprint","IMPRINT",EDGE,{"disambiguationData":[TD([[subQ2,1.0]])],"derivedFrom":subQ1}),1.0]])]});}
            var Q154;
            {var subQ0=sQuery(id+"F1.wireOp",EDGE,"E84");var subQ1=sQuery(id+"F1.wireOp",EDGE,"E2");var subQ2=makeQuery(id+"F1.imprint","INTERSECT",VERTEX,{"derivedFrom":[subQ1,subQ0]});Q154=makeQuery(id+"F1.imprint","IMPRINT",FACE,{"disambiguationData":[TD([[makeQuery(id+"F1.imprint","IMPRINT",EDGE,{"disambiguationData":[TD([[subQ2,-1.0]])],"derivedFrom":subQ1}),1.0]])]});}
            var Q155;
            {var subQ0=sQuery(id+"F1.wireOp",EDGE,"E3");Q155=makeQuery(id+"F1.imprint","IMPRINT",FACE,{"disambiguationData":[TD([[makeQuery(id+"F1.imprint","IMPRINT",EDGE,{"derivedFrom":subQ0}),1.0]])]});}
            var Q156;
            {var subQ0=sQuery(id+"F1.wireOp",EDGE,"E86.trimOffspring");Q156=makeQuery(id+"F1.imprint","IMPRINT",FACE,{"disambiguationData":[TD([[makeQuery(id+"F1.imprint","IMPRINT",EDGE,{"derivedFrom":subQ0}),-1.0]])]});}
            var Q157;
            {var subQ0=sQuery(id+"F1.wireOp",EDGE,"E156.trimOffspring");Q157=makeQuery(id+"F1.imprint","IMPRINT",FACE,{"disambiguationData":[TD([[makeQuery(id+"F1.imprint","IMPRINT",EDGE,{"derivedFrom":subQ0}),1.0]])]});}
            var Q158;
            {var subQ0=sQuery(id+"F1.wireOp",EDGE,"E1");Q158=makeQuery(id+"F1.imprint","IMPRINT",FACE,{"disambiguationData":[TD([[makeQuery(id+"F1.imprint","IMPRINT",EDGE,{"derivedFrom":subQ0}),-1.0]])]});}
            extrude(context, id + "F2", {"entities" : qUnion([Q0, Q1, Q2, Q3, Q4, Q5, Q6, Q7, Q8, Q9, Q10, Q11, Q12, Q13, Q14, Q15, Q16, Q17, Q18, Q19, Q20, Q21, Q22, Q23, Q24, Q25, Q26, Q27, Q28, Q29, Q30, Q31, Q32, Q33, Q34, Q35, Q36, Q37, Q38, Q39, Q40, Q41, Q42, Q43, Q44, Q45, Q46, Q47, Q48, Q49, Q50, Q51, Q52, Q53, Q54, Q55, Q56, Q57, Q58, Q59, Q60, Q61, Q62, Q63, Q64, Q65, Q66, Q67, Q68, Q69, Q70, Q71, Q72, Q73, Q74, Q75, Q76, Q77, Q78, Q79, Q80, Q81, Q82, Q83, Q84, Q85, Q86, Q87, Q88, Q89, Q90, Q91, Q92, Q93, Q94, Q95, Q96, Q97, Q98, Q99, Q100, Q101, Q102, Q103, Q104, Q105, Q106, Q107, Q108, Q109, Q110, Q111, Q112, Q113, Q114, Q115, Q116, Q117, Q118, Q119, Q120, Q121, Q122, Q123, Q124, Q125, Q126, Q127, Q128, Q129, Q130, Q131, Q132, Q133, Q134, Q135, Q136, Q137, Q138, Q139, Q140, Q141, Q142, Q143, Q144, Q145, Q146, Q147, Q148, Q149, Q150, Q151, Q152, Q153, Q154, Q155, Q156, Q157, Q158]), "depth" : 3416 * mm, "offsetDistance" : 25 * mm});
        }
    });
